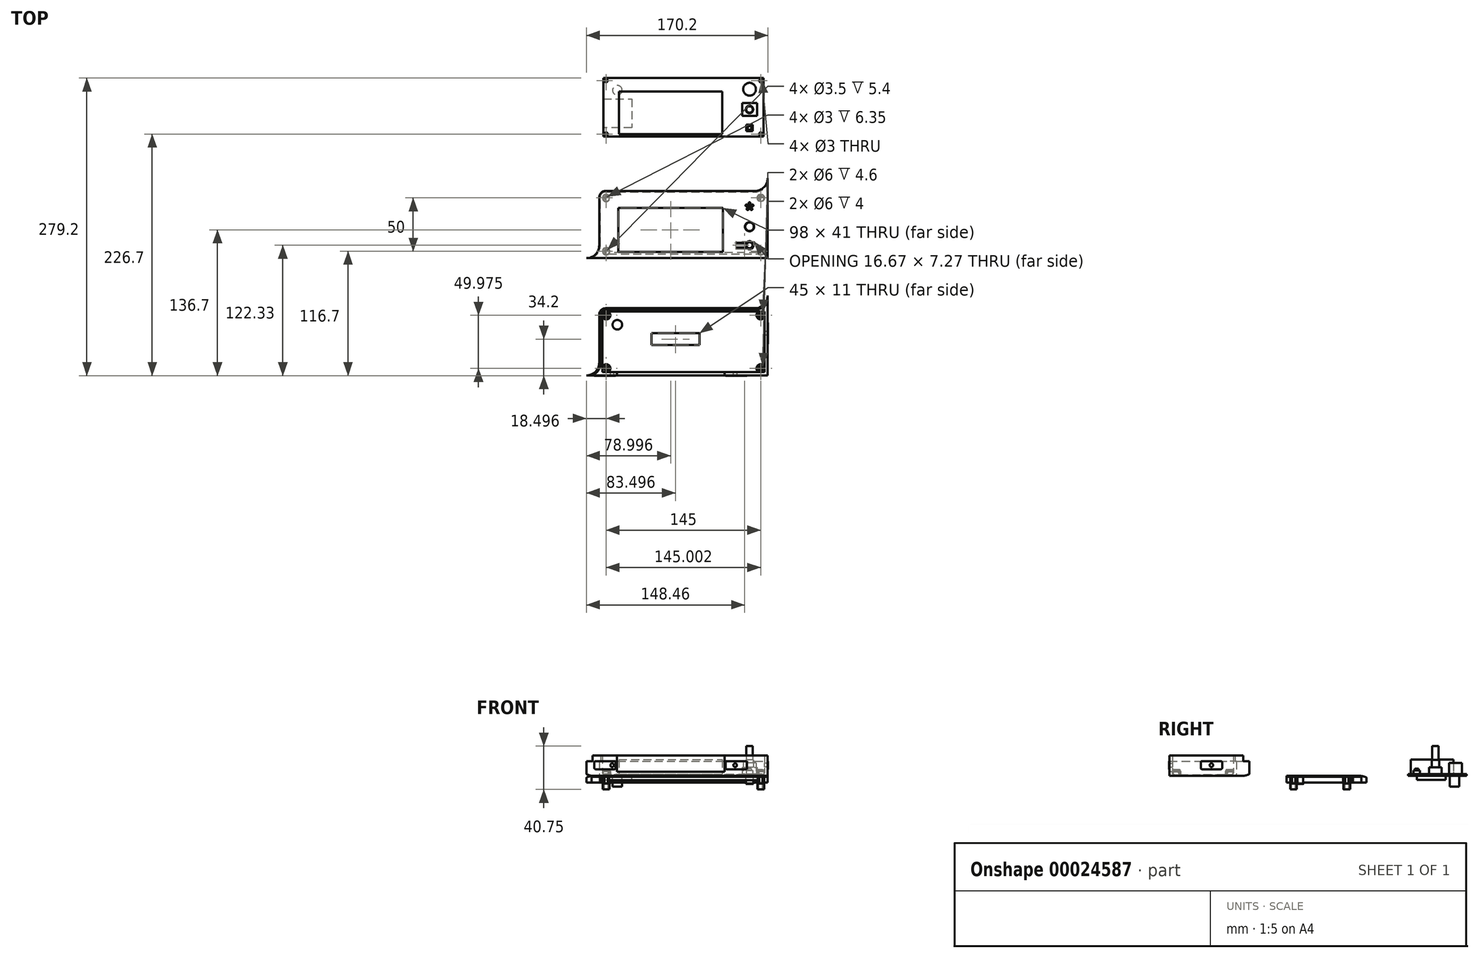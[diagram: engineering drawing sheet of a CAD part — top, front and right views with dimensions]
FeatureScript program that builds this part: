
annotation { "Feature Type Name" : "Feature", "Feature Type Description" : "" }
export const myFeature = defineFeature(function(context is Context, id is Id, definition is map)
    precondition{}
    {
        {
            assignVariable(context, id + "F0", {"name" : "profile_distance_x", "anyValue" : 10 - 7.3 / 2});
        }
        {
            assignVariable(context, id + "F1", {"name" : "plate_thickness", "anyValue" : 1});
        }
        {
            assignVariable(context, id + "F2", {"name" : "lcd_plate_thickness", "anyValue" : 1.5});
        }
        {
            assignVariable(context, id + "F3", {"name" : "lcd_support_dist1", "anyValue" : 10 - 5.5 / 2 - getVariable(context, 'lcd_plate_thickness')});
        }
        {
            assignVariable(context, id + "F4", {"name" : "button_height", "anyValue" : 6.6 - getVariable(context, 'lcd_plate_thickness')});
        }
        {
            var Q0;
            Q0=qCreatedBy(makeId("Top.planeOp"),FACE);
            var sketch = newSketch(context, id + "F5", { "sketchPlane" : qUnion([Q0])});
            skLineSegment(sketch, "E0.bottom", {"start": v(-53.31, -0.5) * mm, "end": v(116.69, -0.5) * mm});
            skLineSegment(sketch, "E0.top", {"start": v(-35.31, 62.5) * mm, "end": v(104.69, 62.5) * mm});
            skLineSegment(sketch, "E0.left", {"start": v(-41.31, 11.5) * mm, "end": v(-41.31, 56.5) * mm});
            skLineSegment(sketch, "E0.right", {"start": v(116.69, -0.5) * mm, "end": v(116.69, 74.5) * mm});
            skArc(sketch, "E1", {"start": v(-53.31, -0.5) * mm, "mid": v(-44.83, 3.01) * mm, "end": v(-41.31, 11.5) * mm});
            skArc(sketch, "E2", {"start": v(-35.31, 62.5) * mm, "mid": v(-39.56, 60.74) * mm, "end": v(-41.31, 56.5) * mm});
            skArc(sketch, "E3", {"start": v(104.69, 62.5) * mm, "mid": v(113.17, 66.01) * mm, "end": v(116.69, 74.5) * mm});
            skLineSegment(sketch, "E4.bottom", {"start": v(-37.31, 58.5) * mm, "end": v(112.69, 58.5) * mm, "construction": true});
            skLineSegment(sketch, "E4.top", {"start": v(-37.31, 3.5) * mm, "end": v(112.69, 3.5) * mm, "construction": true});
            skLineSegment(sketch, "E4.left", {"start": v(-37.31, 58.5) * mm, "end": v(-37.31, 3.5) * mm, "construction": true});
            skLineSegment(sketch, "E4.right", {"start": v(112.69, 58.5) * mm, "end": v(112.69, 3.5) * mm, "construction": true});
            skLineSegment(sketch, "E5", {"start": v(-37.31, 58.5) * mm, "end": v(-37.31, 58.5) * mm});
            skLineSegment(sketch, "E6", {"start": v(37.69, 80.57) * mm, "end": v(37.69, -27.83) * mm, "construction": true});
            skLineSegment(sketch, "E7", {"start": v(-76.03, 31) * mm, "end": v(149.1, 31) * mm, "construction": true});
            skCircle(sketch, "E8", {"center": v(110.19, 56) * mm, "radius": 1.65 * mm});
            skCircle(sketch, "E9.MirrorC", {"center": v(110.19, 6) * mm, "radius": 1.65 * mm});
            skCircle(sketch, "E10.MirrorC", {"center": v(-34.81, 56) * mm, "radius": 1.65 * mm});
            skCircle(sketch, "E11.MirrorC", {"center": v(-34.81, 6) * mm, "radius": 1.65 * mm});
            skLineSegment(sketch, "E12.0", {"start": v(-38.31, 59.5) * mm, "end": v(113.69, 59.5) * mm});
            skLineSegment(sketch, "E12.1", {"start": v(-38.31, 59.5) * mm, "end": v(-38.31, 2.5) * mm});
            skLineSegment(sketch, "E12.2", {"start": v(-38.31, 2.5) * mm, "end": v(113.69, 2.5) * mm});
            skLineSegment(sketch, "E12.3", {"start": v(113.69, 59.5) * mm, "end": v(113.69, 2.5) * mm});
            skCircle(sketch, "E13", {"center": v(-34.81, 56) * mm, "radius": 3.5 * mm});
            skCircle(sketch, "E14", {"center": v(-34.81, 6) * mm, "radius": 3.5 * mm});
            skCircle(sketch, "E15", {"center": v(110.19, 56) * mm, "radius": 3.5 * mm});
            skCircle(sketch, "E16", {"center": v(110.19, 6) * mm, "radius": 3.5 * mm});
            skLineSegment(sketch, "E17", {"start": v(-24.81, 2.5) * mm, "end": v(-24.81, -0.5) * mm});
            skLineSegment(sketch, "E18", {"start": v(76.19, 2.5) * mm, "end": v(76.19, -0.5) * mm});
            skLineSegment(sketch, "E19.bottom", {"start": v(7.69, 39) * mm, "end": v(52.69, 39) * mm});
            skLineSegment(sketch, "E19.top", {"start": v(7.69, 28) * mm, "end": v(52.69, 28) * mm});
            skLineSegment(sketch, "E19.left", {"start": v(7.69, 39) * mm, "end": v(7.69, 28) * mm});
            skLineSegment(sketch, "E19.right", {"start": v(52.69, 39) * mm, "end": v(52.69, 28) * mm});
            skLineSegment(sketch, "E20.0.1.0", {"start": v(-35.31, 172.5) * mm, "end": v(104.69, 172.5) * mm});
            skLineSegment(sketch, "E20.0.1.1", {"start": v(-41.31, 121.5) * mm, "end": v(-41.31, 166.5) * mm});
            skArc(sketch, "E20.0.1.2", {"start": v(-35.31, 172.5) * mm, "mid": v(-39.56, 170.74) * mm, "end": v(-41.31, 166.5) * mm});
            skArc(sketch, "E20.0.1.3", {"start": v(104.69, 172.5) * mm, "mid": v(113.17, 176.01) * mm, "end": v(116.69, 184.5) * mm});
            skLineSegment(sketch, "E20.0.1.4", {"start": v(116.69, 109.5) * mm, "end": v(116.69, 184.5) * mm});
            skLineSegment(sketch, "E20.0.1.5", {"start": v(113.69, 169.5) * mm, "end": v(113.69, 112.5) * mm});
            skLineSegment(sketch, "E20.0.1.6", {"start": v(112.69, 168.5) * mm, "end": v(112.69, 113.5) * mm, "construction": true});
            skLineSegment(sketch, "E20.0.1.7", {"start": v(-37.31, 168.5) * mm, "end": v(112.69, 168.5) * mm, "construction": true});
            skCircle(sketch, "E20.0.1.8", {"center": v(110.19, 166) * mm, "radius": 3.5 * mm});
            skCircle(sketch, "E20.0.1.10", {"center": v(110.19, 116) * mm, "radius": 3.5 * mm});
            skLineSegment(sketch, "E20.0.1.12", {"start": v(-37.31, 113.5) * mm, "end": v(112.69, 113.5) * mm, "construction": true});
            skLineSegment(sketch, "E20.0.1.13", {"start": v(-38.31, 112.5) * mm, "end": v(113.69, 112.5) * mm});
            skLineSegment(sketch, "E20.0.1.14", {"start": v(-53.31, 109.5) * mm, "end": v(116.69, 109.5) * mm});
            skLineSegment(sketch, "E20.0.1.15", {"start": v(-38.31, 169.5) * mm, "end": v(113.69, 169.5) * mm});
            skLineSegment(sketch, "E20.0.1.16", {"start": v(-38.31, 169.5) * mm, "end": v(-38.31, 112.5) * mm});
            skLineSegment(sketch, "E20.0.1.17", {"start": v(-37.31, 168.5) * mm, "end": v(-37.31, 113.5) * mm, "construction": true});
            skCircle(sketch, "E20.0.1.18", {"center": v(-34.81, 166) * mm, "radius": 3.5 * mm});
            skCircle(sketch, "E20.0.1.20", {"center": v(-34.81, 116) * mm, "radius": 3.5 * mm});
            skArc(sketch, "E20.0.1.22", {"start": v(-53.31, 109.5) * mm, "mid": v(-44.83, 113.01) * mm, "end": v(-41.31, 121.5) * mm});
            skLineSegment(sketch, "E20.direction1", {"start": v(-35.31, 62.5) * mm, "end": v(-4, 62.5) * mm, "construction": true});
            skLineSegment(sketch, "E20.direction2", {"start": v(-35.31, 62.5) * mm, "end": v(-35.31, 172.5) * mm, "construction": true});
            skLineSegment(sketch, "E21.bottom", {"start": v(-22.81, 156) * mm, "end": v(74.19, 156) * mm, "construction": true});
            skLineSegment(sketch, "E21.top", {"start": v(-22.81, 116) * mm, "end": v(74.19, 116) * mm, "construction": true});
            skLineSegment(sketch, "E21.left", {"start": v(-22.81, 156) * mm, "end": v(-22.81, 116) * mm, "construction": true});
            skLineSegment(sketch, "E21.right", {"start": v(74.19, 156) * mm, "end": v(74.19, 116) * mm, "construction": true});
            skCircle(sketch, "E22", {"center": v(99.69, 139) * mm, "radius": 4 * mm});
            skLineSegment(sketch, "E23.bottom", {"start": v(96.69, 124.63) * mm, "end": v(102.69, 124.63) * mm, "construction": true});
            skLineSegment(sketch, "E23.top", {"start": v(96.69, 118.63) * mm, "end": v(102.69, 118.63) * mm, "construction": true});
            skLineSegment(sketch, "E23.left", {"start": v(96.69, 124.63) * mm, "end": v(96.69, 118.63) * mm, "construction": true});
            skLineSegment(sketch, "E23.right", {"start": v(102.69, 124.63) * mm, "end": v(102.69, 118.63) * mm, "construction": true});
            skCircle(sketch, "E24", {"center": v(99.69, 121.63) * mm, "radius": 1.75 * mm, "construction": true});
            skLineSegment(sketch, "E25", {"start": v(96.69, 121.63) * mm, "end": v(102.69, 121.63) * mm, "construction": true});
            skLineSegment(sketch, "E26", {"start": v(99.69, 124.63) * mm, "end": v(99.69, 118.63) * mm, "construction": true});
            skCircle(sketch, "E27", {"center": v(99.69, 161) * mm, "radius": 0.6 * mm});
            skCircle(sketch, "E28.1.0", {"center": v(96.83, 158.93) * mm, "radius": 0.6 * mm});
            skCircle(sketch, "E28.2.0", {"center": v(97.92, 155.57) * mm, "radius": 0.6 * mm});
            skCircle(sketch, "E28.3.0", {"center": v(101.45, 155.57) * mm, "radius": 0.6 * mm});
            skCircle(sketch, "E28.4.0", {"center": v(102.54, 158.93) * mm, "radius": 0.6 * mm});
            skPoint(sketch, "E28.center", {"position": v(99.69, 158) * mm});
            skLineSegment(sketch, "E29", {"start": v(99.69, 124.63) * mm, "end": v(99.69, 182.09) * mm, "construction": true});
            skCircle(sketch, "E30", {"center": v(99.69, 158) * mm, "radius": 3 * mm, "construction": true});
            skCircle(sketch, "E31", {"center": v(-34.81, 166) * mm, "radius": 1.5 * mm});
            skCircle(sketch, "E32", {"center": v(-34.81, 116) * mm, "radius": 1.5 * mm});
            skCircle(sketch, "E33", {"center": v(110.19, 166) * mm, "radius": 1.5 * mm});
            skCircle(sketch, "E34", {"center": v(110.19, 116) * mm, "radius": 1.5 * mm});
            skLineSegment(sketch, "E35.bottom", {"start": v(96.81, 123.63) * mm, "end": v(86.81, 123.63) * mm});
            skLineSegment(sketch, "E35.top", {"start": v(96.81, 119.63) * mm, "end": v(86.81, 119.63) * mm});
            skLineSegment(sketch, "E35.left", {"start": v(96.81, 123.63) * mm, "end": v(96.81, 119.63) * mm, "construction": true});
            skPoint(sketch, "E36", {"position": v(96.81, 121.63) * mm});
            skArc(sketch, "E37", {"start": v(96.81, 119.63) * mm, "mid": v(103.19, 121.63) * mm, "end": v(96.81, 123.63) * mm});
            skLineSegment(sketch, "E38.0", {"start": v(96.66, 123.93) * mm, "end": v(86.81, 123.93) * mm});
            skArc(sketch, "E38.1", {"start": v(96.66, 119.33) * mm, "mid": v(103.49, 121.63) * mm, "end": v(96.66, 123.93) * mm});
            skLineSegment(sketch, "E38.2", {"start": v(96.66, 119.33) * mm, "end": v(86.81, 119.33) * mm});
            skLineSegment(sketch, "E39", {"start": v(86.81, 123.63) * mm, "end": v(86.81, 123.93) * mm});
            skLineSegment(sketch, "E40", {"start": v(86.81, 119.33) * mm, "end": v(86.81, 119.63) * mm});
            skArc(sketch, "E41", {"start": v(96.81, 123.63) * mm, "mid": v(96.19, 121.63) * mm, "end": v(96.81, 119.63) * mm});
            skLineSegment(sketch, "E42.0", {"start": v(-23.31, 156.5) * mm, "end": v(74.69, 156.5) * mm});
            skLineSegment(sketch, "E42.1", {"start": v(-23.31, 156.5) * mm, "end": v(-23.31, 115.5) * mm});
            skLineSegment(sketch, "E42.2", {"start": v(-23.31, 115.5) * mm, "end": v(74.69, 115.5) * mm});
            skLineSegment(sketch, "E42.3", {"start": v(74.69, 156.5) * mm, "end": v(74.69, 115.5) * mm});
            skPoint(sketch, "E43.0.1.0", {"position": v(99.69, 268) * mm});
            skCircle(sketch, "E43.0.1.1", {"center": v(110.19, 276) * mm, "radius": 1.5 * mm});
            skCircle(sketch, "E43.0.1.2", {"center": v(110.19, 226) * mm, "radius": 1.5 * mm});
            skCircle(sketch, "E43.0.1.3", {"center": v(-34.81, 276) * mm, "radius": 1.5 * mm});
            skCircle(sketch, "E43.0.1.4", {"center": v(-34.81, 226) * mm, "radius": 1.5 * mm});
            skLineSegment(sketch, "E43.0.1.5", {"start": v(99.69, 234.63) * mm, "end": v(99.69, 228.63) * mm, "construction": true});
            skLineSegment(sketch, "E43.0.1.6", {"start": v(96.69, 231.63) * mm, "end": v(102.69, 231.63) * mm, "construction": true});
            skCircle(sketch, "E43.0.1.7", {"center": v(99.69, 249) * mm, "radius": 4 * mm, "construction": true});
            skLineSegment(sketch, "E43.0.1.8", {"start": v(-37.31, 278.5) * mm, "end": v(112.69, 278.5) * mm, "construction": true});
            skLineSegment(sketch, "E43.0.1.9", {"start": v(-37.31, 223.5) * mm, "end": v(112.69, 223.5) * mm, "construction": true});
            skLineSegment(sketch, "E43.0.1.10", {"start": v(-22.81, 266) * mm, "end": v(74.19, 266) * mm, "construction": true});
            skLineSegment(sketch, "E43.0.1.11", {"start": v(-22.81, 226) * mm, "end": v(74.19, 226) * mm, "construction": true});
            skLineSegment(sketch, "E43.direction1", {"start": v(-34.81, 116) * mm, "end": v(-9.81, 116) * mm, "construction": true});
            skLineSegment(sketch, "E43.direction2", {"start": v(-34.81, 116) * mm, "end": v(-34.81, 226) * mm, "construction": true});
            skLineSegment(sketch, "E44.bottom", {"start": v(-37.31, 278.5) * mm, "end": v(112.69, 278.5) * mm});
            skLineSegment(sketch, "E44.top", {"start": v(-37.31, 223.5) * mm, "end": v(112.69, 223.5) * mm});
            skLineSegment(sketch, "E44.left", {"start": v(-37.31, 278.5) * mm, "end": v(-37.31, 223.5) * mm});
            skLineSegment(sketch, "E44.right", {"start": v(112.69, 278.5) * mm, "end": v(112.69, 223.5) * mm});
            skLineSegment(sketch, "E45.bottom", {"start": v(-22.81, 266) * mm, "end": v(74.19, 266) * mm});
            skLineSegment(sketch, "E45.top", {"start": v(-22.81, 226) * mm, "end": v(74.19, 226) * mm});
            skLineSegment(sketch, "E45.left", {"start": v(-22.81, 266) * mm, "end": v(-22.81, 226) * mm});
            skLineSegment(sketch, "E45.right", {"start": v(74.19, 266) * mm, "end": v(74.19, 226) * mm});
            skLineSegment(sketch, "E46.bottom", {"start": v(96.69, 234.63) * mm, "end": v(102.69, 234.63) * mm});
            skLineSegment(sketch, "E46.top", {"start": v(96.69, 228.63) * mm, "end": v(102.69, 228.63) * mm});
            skLineSegment(sketch, "E46.left", {"start": v(96.69, 234.63) * mm, "end": v(96.69, 228.63) * mm});
            skLineSegment(sketch, "E46.right", {"start": v(102.69, 234.63) * mm, "end": v(102.69, 228.63) * mm});
            skCircle(sketch, "E47", {"center": v(99.69, 231.63) * mm, "radius": 1.75 * mm});
            skCircle(sketch, "E48", {"center": v(99.69, 268) * mm, "radius": 6 * mm});
            skLineSegment(sketch, "E49.bottom", {"start": v(92.69, 255) * mm, "end": v(106.69, 255) * mm});
            skLineSegment(sketch, "E49.top", {"start": v(92.69, 243) * mm, "end": v(106.69, 243) * mm});
            skLineSegment(sketch, "E49.left", {"start": v(92.69, 255) * mm, "end": v(92.69, 243) * mm});
            skLineSegment(sketch, "E49.right", {"start": v(106.69, 255) * mm, "end": v(106.69, 243) * mm});
            skLineSegment(sketch, "E50", {"start": v(99.69, 255) * mm, "end": v(99.69, 243) * mm, "construction": true});
            skLineSegment(sketch, "E51", {"start": v(106.69, 249) * mm, "end": v(92.69, 249) * mm, "construction": true});
            skCircle(sketch, "E52", {"center": v(99.69, 249) * mm, "radius": 3.5 * mm});
            skCircle(sketch, "E53", {"center": v(99.69, 249) * mm, "radius": 3 * mm});
            skLineSegment(sketch, "E54", {"start": v(-37.31, 258.8) * mm, "end": v(-10.81, 258.8) * mm});
            skLineSegment(sketch, "E55", {"start": v(-10.81, 258.8) * mm, "end": v(-10.81, 231.8) * mm});
            skLineSegment(sketch, "E56", {"start": v(-10.81, 231.8) * mm, "end": v(-37.31, 231.8) * mm});
            skCircle(sketch, "E57", {"center": v(-24.31, 267) * mm, "radius": 4.5 * mm});
            skCircle(sketch, "E58", {"center": v(-24.31, 47) * mm, "radius": 4.5 * mm});
            skCircle(sketch, "E59", {"center": v(99.69, 158) * mm, "radius": 0.6 * mm});
            skLineSegment(sketch, "E60.0", {"start": v(-37.91, 169.1) * mm, "end": v(113.29, 169.1) * mm});
            skLineSegment(sketch, "E60.1", {"start": v(-37.91, 169.1) * mm, "end": v(-37.91, 112.9) * mm});
            skLineSegment(sketch, "E60.2", {"start": v(-37.91, 112.9) * mm, "end": v(113.29, 112.9) * mm});
            skLineSegment(sketch, "E60.3", {"start": v(113.29, 169.1) * mm, "end": v(113.29, 112.9) * mm});
            skLineSegment(sketch, "E61", {"start": v(-32.36, 113.5) * mm, "end": v(107.74, 113.5) * mm});
            skLineSegment(sketch, "E62", {"start": v(106.94, 114.7) * mm, "end": v(-31.56, 114.7) * mm});
            skSolve(sketch);
        }
        {
            var Q0;
            Q0=makeQuery(id+"F5.imprint","IMPRINT",FACE,{"disambiguationData":[TD([[makeQuery(id+"F5.imprint","IMPRINT",EDGE,{"derivedFrom":sQuery(id+"F5.wireOp",EDGE,"E0.bottom")}),1.0]])]});
            var Q1;
            Q1=makeQuery(id+"F5.imprint","IMPRINT",FACE,{"disambiguationData":[TD([[makeQuery(id+"F5.imprint","IMPRINT",EDGE,{"derivedFrom":sQuery(id+"F5.wireOp",EDGE,"E8")}),-1.0]])]});
            var Q2;
            {var subQ5=sQuery(id+"F5.wireOp",EDGE,"E12.0");var subQ11=sQuery(id+"F5.wireOp",EDGE,"E13");var subQ15=makeQuery(id+"F5.imprint","INTERSECT",VERTEX,{"derivedFrom":[subQ5,subQ11]});Q2=makeQuery(id+"F5.imprint","IMPRINT",FACE,{"disambiguationData":[TD([[makeQuery(id+"F5.imprint","IMPRINT",EDGE,{"disambiguationData":[TD([[subQ15,-1.0]])],"derivedFrom":subQ5}),-1.0]])]});}
            var Q3;
            Q3=makeQuery(id+"F5.imprint","IMPRINT",FACE,{"disambiguationData":[TD([[makeQuery(id+"F5.imprint","IMPRINT",EDGE,{"derivedFrom":sQuery(id+"F5.wireOp",EDGE,"E10.MirrorC")}),1.0]])]});
            var Q4;
            {var subQ0=sQuery(id+"F5.wireOp",EDGE,"E12.1");var subQ1=sQuery(id+"F5.wireOp",EDGE,"E12.0");var subQ2=makeQuery(id+"F5.imprint","INTERSECT",VERTEX,{"derivedFrom":[subQ1,subQ0]});Q4=makeQuery(id+"F5.imprint","IMPRINT",FACE,{"disambiguationData":[TD([[makeQuery(id+"F5.imprint","IMPRINT",EDGE,{"disambiguationData":[TD([[subQ2,-1.0]])],"derivedFrom":subQ1}),-1.0]])]});}
            var Q5;
            {var subQ0=sQuery(id+"F5.wireOp",EDGE,"E12.2");var subQ1=sQuery(id+"F5.wireOp",EDGE,"E12.1");var subQ2=makeQuery(id+"F5.imprint","INTERSECT",VERTEX,{"derivedFrom":[subQ1,subQ0]});Q5=makeQuery(id+"F5.imprint","IMPRINT",FACE,{"disambiguationData":[TD([[makeQuery(id+"F5.imprint","IMPRINT",EDGE,{"disambiguationData":[TD([[subQ2,1.0]])],"derivedFrom":subQ1}),1.0]])]});}
            var Q6;
            Q6=makeQuery(id+"F5.imprint","IMPRINT",FACE,{"disambiguationData":[TD([[makeQuery(id+"F5.imprint","IMPRINT",EDGE,{"derivedFrom":sQuery(id+"F5.wireOp",EDGE,"E11.MirrorC")}),-1.0]])]});
            var Q7;
            {var subQ0=sQuery(id+"F5.wireOp",EDGE,"E12.3");var subQ1=sQuery(id+"F5.wireOp",EDGE,"E12.0");var subQ2=makeQuery(id+"F5.imprint","INTERSECT",VERTEX,{"derivedFrom":[subQ1,subQ0]});Q7=makeQuery(id+"F5.imprint","IMPRINT",FACE,{"disambiguationData":[TD([[makeQuery(id+"F5.imprint","IMPRINT",EDGE,{"disambiguationData":[TD([[subQ2,1.0]])],"derivedFrom":subQ1}),-1.0]])]});}
            var Q8;
            Q8=makeQuery(id+"F5.imprint","IMPRINT",FACE,{"disambiguationData":[TD([[makeQuery(id+"F5.imprint","IMPRINT",EDGE,{"derivedFrom":sQuery(id+"F5.wireOp",EDGE,"E9.MirrorC")}),1.0]])]});
            var Q9;
            {var subQ0=sQuery(id+"F5.wireOp",EDGE,"E12.3");var subQ1=sQuery(id+"F5.wireOp",EDGE,"E12.2");var subQ2=makeQuery(id+"F5.imprint","INTERSECT",VERTEX,{"derivedFrom":[subQ1,subQ0]});Q9=makeQuery(id+"F5.imprint","IMPRINT",FACE,{"disambiguationData":[TD([[makeQuery(id+"F5.imprint","IMPRINT",EDGE,{"disambiguationData":[TD([[subQ2,1.0]])],"derivedFrom":subQ1}),1.0]])]});}
            var Q10;
            {var subQ0=sQuery(id+"F5.wireOp",EDGE,"E17");Q10=makeQuery(id+"F5.imprint","IMPRINT",FACE,{"disambiguationData":[TD([[makeQuery(id+"F5.imprint","IMPRINT",EDGE,{"derivedFrom":subQ0}),1.0]])]});}
            extrude(context, id + "F6", {"entities" : qUnion([Q0, Q1, Q2, Q3, Q4, Q5, Q6, Q7, Q8, Q9, Q10]), "depth" : (getVariable(context, 'plate_thickness')) * mm});
        }
        {
            var Q0;
            Q0=makeQuery(id+"F5.imprint","IMPRINT",FACE,{"disambiguationData":[TD([[makeQuery(id+"F5.imprint","IMPRINT",EDGE,{"derivedFrom":sQuery(id+"F5.wireOp",EDGE,"E0.bottom")}),1.0]])]});
            extrude(context, id + "F7", {"entities" : qUnion([Q0]), "operationType" : NewBodyOperationType.ADD, "depth" : (20 - getVariable(context, 'profile_distance_x')) * mm});
        }
        {
            var Q0;
            {var subQ0=sQuery(id+"F5.wireOp",EDGE,"E17");Q0=makeQuery(id+"F5.imprint","IMPRINT",FACE,{"disambiguationData":[TD([[makeQuery(id+"F5.imprint","IMPRINT",EDGE,{"derivedFrom":subQ0}),1.0]])]});}
            extrude(context, id + "F8", {"entities" : qUnion([Q0]), "operationType" : NewBodyOperationType.ADD, "depth" : 4 * mm});
        }
        {
            var Q0;
            {var subQ0=sQuery(id+"F5.wireOp",EDGE,"E12.3");var subQ1=sQuery(id+"F5.wireOp",EDGE,"E12.2");var subQ2=makeQuery(id+"F5.imprint","INTERSECT",VERTEX,{"derivedFrom":[subQ1,subQ0]});Q0=makeQuery(id+"F5.imprint","IMPRINT",FACE,{"disambiguationData":[TD([[makeQuery(id+"F5.imprint","IMPRINT",EDGE,{"disambiguationData":[TD([[subQ2,1.0]])],"derivedFrom":subQ1}),1.0]])]});}
            var Q1;
            Q1=makeQuery(id+"F5.imprint","IMPRINT",FACE,{"disambiguationData":[TD([[makeQuery(id+"F5.imprint","IMPRINT",EDGE,{"derivedFrom":sQuery(id+"F5.wireOp",EDGE,"E9.MirrorC")}),1.0]])]});
            var Q2;
            {var subQ0=sQuery(id+"F5.wireOp",EDGE,"E12.3");var subQ1=sQuery(id+"F5.wireOp",EDGE,"E12.0");var subQ2=makeQuery(id+"F5.imprint","INTERSECT",VERTEX,{"derivedFrom":[subQ1,subQ0]});Q2=makeQuery(id+"F5.imprint","IMPRINT",FACE,{"disambiguationData":[TD([[makeQuery(id+"F5.imprint","IMPRINT",EDGE,{"disambiguationData":[TD([[subQ2,1.0]])],"derivedFrom":subQ1}),-1.0]])]});}
            var Q3;
            Q3=makeQuery(id+"F5.imprint","IMPRINT",FACE,{"disambiguationData":[TD([[makeQuery(id+"F5.imprint","IMPRINT",EDGE,{"derivedFrom":sQuery(id+"F5.wireOp",EDGE,"E8")}),-1.0]])]});
            var Q4;
            Q4=makeQuery(id+"F5.imprint","IMPRINT",FACE,{"disambiguationData":[TD([[makeQuery(id+"F5.imprint","IMPRINT",EDGE,{"derivedFrom":sQuery(id+"F5.wireOp",EDGE,"E10.MirrorC")}),1.0]])]});
            var Q5;
            {var subQ0=sQuery(id+"F5.wireOp",EDGE,"E12.1");var subQ1=sQuery(id+"F5.wireOp",EDGE,"E12.0");var subQ2=makeQuery(id+"F5.imprint","INTERSECT",VERTEX,{"derivedFrom":[subQ1,subQ0]});Q5=makeQuery(id+"F5.imprint","IMPRINT",FACE,{"disambiguationData":[TD([[makeQuery(id+"F5.imprint","IMPRINT",EDGE,{"disambiguationData":[TD([[subQ2,-1.0]])],"derivedFrom":subQ1}),-1.0]])]});}
            var Q6;
            {var subQ0=sQuery(id+"F5.wireOp",EDGE,"E12.2");var subQ1=sQuery(id+"F5.wireOp",EDGE,"E12.1");var subQ2=makeQuery(id+"F5.imprint","INTERSECT",VERTEX,{"derivedFrom":[subQ1,subQ0]});Q6=makeQuery(id+"F5.imprint","IMPRINT",FACE,{"disambiguationData":[TD([[makeQuery(id+"F5.imprint","IMPRINT",EDGE,{"disambiguationData":[TD([[subQ2,1.0]])],"derivedFrom":subQ1}),1.0]])]});}
            var Q7;
            Q7=makeQuery(id+"F5.imprint","IMPRINT",FACE,{"disambiguationData":[TD([[makeQuery(id+"F5.imprint","IMPRINT",EDGE,{"derivedFrom":sQuery(id+"F5.wireOp",EDGE,"E11.MirrorC")}),-1.0]])]});
            extrude(context, id + "F9", {"entities" : qUnion([Q0, Q1, Q2, Q3, Q4, Q5, Q6, Q7]), "operationType" : NewBodyOperationType.ADD, "depth" : (getVariable(context, 'lcd_support_dist1')) * mm});
        }
        {
            var Q0;
            Q0=makeQuery(id+"F7.opExtrude","CAP_FACE",FACE,{"disambiguationData":[OSD([sQuery(id+"F5.wireOp",EDGE,"E0.bottom"),sQuery(id+"F5.wireOp",EDGE,"E0.top"),sQuery(id+"F5.wireOp",EDGE,"E0.left"),sQuery(id+"F5.wireOp",EDGE,"E0.right"),sQuery(id+"F5.wireOp",EDGE,"E1"),sQuery(id+"F5.wireOp",EDGE,"E2"),sQuery(id+"F5.wireOp",EDGE,"E3"),sQuery(id+"F5.wireOp",EDGE,"E12.0"),sQuery(id+"F5.wireOp",EDGE,"E12.1"),sQuery(id+"F5.wireOp",EDGE,"E12.2"),sQuery(id+"F5.wireOp",EDGE,"E12.3"),sQuery(id+"F5.wireOp",EDGE,"E17"),sQuery(id+"F5.wireOp",EDGE,"E18")])],"isStart":false});
            var sketch = newSketch(context, id + "F10", { "sketchPlane" : qUnion([Q0])});
            skLineSegment(sketch, "E63.0", {"start": v(-35.31, 62.5) * mm, "end": v(104.69, 62.5) * mm, "construction": true});
            skArc(sketch, "E64.0", {"start": v(-35.31, 62.5) * mm, "mid": v(-39.56, 60.74) * mm, "end": v(-41.31, 56.5) * mm, "construction": true});
            skLineSegment(sketch, "E65.0", {"start": v(-41.31, 11.5) * mm, "end": v(-41.31, 56.5) * mm, "construction": true});
            skArc(sketch, "E66.0", {"start": v(-53.31, -0.5) * mm, "mid": v(-44.83, 3.01) * mm, "end": v(-41.31, 11.5) * mm, "construction": true});
            skArc(sketch, "E67.0", {"start": v(104.69, 62.5) * mm, "mid": v(113.17, 66.01) * mm, "end": v(116.69, 74.5) * mm, "construction": true});
            skArc(sketch, "E68.0", {"start": v(104.69, 61.2) * mm, "mid": v(114.1, 65.1) * mm, "end": v(117.99, 74.5) * mm});
            skArc(sketch, "E68.1", {"start": v(-53.31, -1.8) * mm, "mid": v(-43.9, 2.1) * mm, "end": v(-40.01, 11.5) * mm});
            skLineSegment(sketch, "E68.2", {"start": v(-40.01, 11.5) * mm, "end": v(-40.01, 56.5) * mm});
            skArc(sketch, "E68.3", {"start": v(-35.31, 61.2) * mm, "mid": v(-38.64, 59.82) * mm, "end": v(-40.01, 56.5) * mm});
            skLineSegment(sketch, "E68.4", {"start": v(-35.31, 61.2) * mm, "end": v(104.69, 61.2) * mm});
            skSolve(sketch);
        }
        {
            var Q0;
            {var subQ15=sQuery(id+"F10.wireOp",EDGE,"E68.2");Q0=makeQuery(id+"F10.imprint","IMPRINT",FACE,{"disambiguationData":[TD([[makeQuery(id+"F10.imprint","IMPRINT",EDGE,{"derivedFrom":subQ15}),-1.0]])]});}
            extrude(context, id + "F11", {"entities" : qUnion([Q0]), "operationType" : NewBodyOperationType.ADD, "depth" : (getVariable(context, 'profile_distance_x') - getVariable(context, 'plate_thickness')) * mm});
        }
        {
            var Q0;
            {var subQ0=sQuery(id+"F5.wireOp",EDGE,"E0.bottom");Q0=makeQuery(id+"F7.boolean.opBoolean","MERGE",FACE,{"derivedFrom":[makeQuery(id+"F6.opExtrude","SWEPT_FACE",FACE,{"disambiguationData":[OSD([subQ0])]}),makeQuery(id+"F7.opExtrude","SWEPT_FACE",FACE,{"disambiguationData":[OSD([subQ0])]})]});}
            var sketch = newSketch(context, id + "F12", { "sketchPlane" : qUnion([Q0])});
            skCircle(sketch, "E69", {"center": v(-29.16, 10) * mm, "radius": 1.7 * mm});
            skCircle(sketch, "E70", {"center": v(86.19, 10) * mm, "radius": 1.7 * mm});
            skCircle(sketch, "E71", {"center": v(-29.16, 10) * mm, "radius": 3 * mm, "construction": true});
            skLineSegment(sketch, "E72", {"start": v(-23.5, 10) * mm, "end": v(-50.14, 10) * mm, "construction": true});
            skLineSegment(sketch, "E73.bottom", {"start": v(-45.81, 13.75) * mm, "end": v(-25.81, 13.75) * mm});
            skLineSegment(sketch, "E73.top", {"start": v(-45.81, 6.25) * mm, "end": v(-25.81, 6.25) * mm});
            skLineSegment(sketch, "E73.left", {"start": v(-45.81, 13.75) * mm, "end": v(-45.81, 6.25) * mm});
            skLineSegment(sketch, "E73.right", {"start": v(-25.81, 13.75) * mm, "end": v(-25.81, 6.25) * mm});
            skPoint(sketch, "E74", {"position": v(-45.81, 10) * mm});
            skPoint(sketch, "E74.positionSnap0", {"position": v(-45.81, 10) * mm});
            skPoint(sketch, "E75.visualSharp", {"position": v(-45.81, 13.75) * mm});
            skPoint(sketch, "E76.visualSharp", {"position": v(-25.81, 13.75) * mm});
            skPoint(sketch, "E77.visualSharp", {"position": v(-25.81, 6.25) * mm});
            skPoint(sketch, "E78.visualSharp", {"position": v(-45.81, 6.25) * mm});
            skLineSegment(sketch, "E79.bottom", {"start": v(77.19, 13.75) * mm, "end": v(97.19, 13.75) * mm});
            skLineSegment(sketch, "E79.top", {"start": v(77.19, 6.25) * mm, "end": v(97.19, 6.25) * mm});
            skLineSegment(sketch, "E79.left", {"start": v(77.19, 13.75) * mm, "end": v(77.19, 6.25) * mm});
            skLineSegment(sketch, "E79.right", {"start": v(97.19, 13.75) * mm, "end": v(97.19, 6.25) * mm});
            skLineSegment(sketch, "E80", {"start": v(75.4, 10) * mm, "end": v(102.6, 10) * mm, "construction": true});
            skPoint(sketch, "E81", {"position": v(77.19, 10) * mm});
            skLineSegment(sketch, "E82.0", {"start": v(-36.46, 0) * mm, "end": v(-33.16, 0) * mm, "construction": true});
            skLineSegment(sketch, "E83", {"start": v(-33.16, 0) * mm, "end": v(-33.16, 11.92) * mm, "construction": true});
            skSolve(sketch);
        }
        {
            var Q0;
            Q0=makeQuery(id+"F12.imprint","IMPRINT",FACE,{"disambiguationData":[TD([[makeQuery(id+"F12.imprint","IMPRINT",EDGE,{"derivedFrom":sQuery(id+"F12.wireOp",EDGE,"E69")}),-1.0]])]});
            var Q1;
            Q1=makeQuery(id+"F12.imprint","IMPRINT",FACE,{"disambiguationData":[TD([[makeQuery(id+"F12.imprint","IMPRINT",EDGE,{"derivedFrom":sQuery(id+"F12.wireOp",EDGE,"E70")}),-1.0]])]});
            extrude(context, id + "F13", {"entities" : qUnion([Q0, Q1]), "operationType" : NewBodyOperationType.ADD, "depth" : 0.2 * mm});
        }
        {
            var Q0;
            Q0=makeQuery(id+"F12.imprint","IMPRINT",FACE,{"disambiguationData":[TD([[makeQuery(id+"F12.imprint","IMPRINT",EDGE,{"derivedFrom":sQuery(id+"F12.wireOp",EDGE,"E69")}),1.0]])]});
            var Q1;
            Q1=makeQuery(id+"F12.imprint","IMPRINT",FACE,{"disambiguationData":[TD([[makeQuery(id+"F12.imprint","IMPRINT",EDGE,{"derivedFrom":sQuery(id+"F12.wireOp",EDGE,"E70")}),1.0]])]});
            extrude(context, id + "F14", {"entities" : qUnion([Q0, Q1]), "operationType" : NewBodyOperationType.REMOVE, "endBound" : BoundingType.UP_TO_NEXT, "oppositeDirection" : true, "depth" : 25 * mm});
        }
        {
            var Q0;
            {var subQ0=sQuery(id+"F5.wireOp",EDGE,"E0.right");Q0=makeQuery(id+"F7.boolean.opBoolean","MERGE",FACE,{"derivedFrom":[makeQuery(id+"F6.opExtrude","SWEPT_FACE",FACE,{"disambiguationData":[OSD([subQ0])]}),makeQuery(id+"F7.opExtrude","SWEPT_FACE",FACE,{"disambiguationData":[OSD([subQ0])]})]});}
            var sketch = newSketch(context, id + "F15", { "sketchPlane" : qUnion([Q0])});
            skPoint(sketch, "E84", {"position": v(56, 0) * mm});
            skLineSegment(sketch, "E85", {"start": v(56, -1.1) * mm, "end": v(56, 19.44) * mm, "construction": true});
            skCircle(sketch, "E86", {"center": v(39, 10) * mm, "radius": 1.7 * mm});
            skLineSegment(sketch, "E87", {"start": v(27.9, 10) * mm, "end": v(50.63, 10) * mm, "construction": true});
            skLineSegment(sketch, "E88", {"start": v(39, 14.69) * mm, "end": v(39, 5.42) * mm, "construction": true});
            skLineSegment(sketch, "E89.bottom", {"start": v(29, 13.75) * mm, "end": v(49, 13.75) * mm});
            skLineSegment(sketch, "E89.top", {"start": v(29, 6.25) * mm, "end": v(49, 6.25) * mm});
            skLineSegment(sketch, "E89.left", {"start": v(29, 13.75) * mm, "end": v(29, 6.25) * mm});
            skLineSegment(sketch, "E89.right", {"start": v(49, 13.75) * mm, "end": v(49, 6.25) * mm});
            skPoint(sketch, "E90", {"position": v(29, 10) * mm});
            skPoint(sketch, "E91", {"position": v(39, 13.75) * mm});
            skLineSegment(sketch, "E92.0", {"start": v(54.35, 0) * mm, "end": v(57.65, 0) * mm, "construction": true});
            skSolve(sketch);
        }
        {
            var Q0;
            Q0=makeQuery(id+"F15.imprint","IMPRINT",FACE,{"disambiguationData":[TD([[makeQuery(id+"F15.imprint","IMPRINT",EDGE,{"derivedFrom":sQuery(id+"F15.wireOp",EDGE,"E86")}),-1.0]])]});
            extrude(context, id + "F16", {"entities" : qUnion([Q0]), "operationType" : NewBodyOperationType.ADD, "depth" : 0.2 * mm});
        }
        {
            var Q0;
            Q0=makeQuery(id+"F15.imprint","IMPRINT",FACE,{"disambiguationData":[TD([[makeQuery(id+"F15.imprint","IMPRINT",EDGE,{"derivedFrom":sQuery(id+"F15.wireOp",EDGE,"E86")}),1.0]])]});
            extrude(context, id + "F17", {"entities" : qUnion([Q0]), "operationType" : NewBodyOperationType.REMOVE, "endBound" : BoundingType.UP_TO_NEXT, "oppositeDirection" : true, "depth" : 25 * mm});
        }
        {
            var Q0;
            Q0=makeQuery(id+"F13.opExtrude","SWEPT_EDGE",EDGE,{"disambiguationData":[OSD([sQuery(id+"F12.wireOp",EDGE,"E73.bottom"),sQuery(id+"F12.wireOp",EDGE,"E73.left")])]});
            var Q1;
            Q1=makeQuery(id+"F13.opExtrude","SWEPT_EDGE",EDGE,{"disambiguationData":[OSD([sQuery(id+"F12.wireOp",EDGE,"E73.top"),sQuery(id+"F12.wireOp",EDGE,"E73.left")])]});
            var Q2;
            Q2=makeQuery(id+"F13.opExtrude","SWEPT_EDGE",EDGE,{"disambiguationData":[OSD([sQuery(id+"F12.wireOp",EDGE,"E73.top"),sQuery(id+"F12.wireOp",EDGE,"E73.right")])]});
            var Q3;
            Q3=makeQuery(id+"F13.opExtrude","SWEPT_EDGE",EDGE,{"disambiguationData":[OSD([sQuery(id+"F12.wireOp",EDGE,"E73.bottom"),sQuery(id+"F12.wireOp",EDGE,"E73.right")])]});
            var Q4;
            Q4=makeQuery(id+"F13.opExtrude","SWEPT_EDGE",EDGE,{"disambiguationData":[OSD([sQuery(id+"F12.wireOp",EDGE,"E79.top"),sQuery(id+"F12.wireOp",EDGE,"E79.right")])]});
            var Q5;
            Q5=makeQuery(id+"F13.opExtrude","SWEPT_EDGE",EDGE,{"disambiguationData":[OSD([sQuery(id+"F12.wireOp",EDGE,"E79.bottom"),sQuery(id+"F12.wireOp",EDGE,"E79.right")])]});
            var Q6;
            Q6=makeQuery(id+"F13.opExtrude","SWEPT_EDGE",EDGE,{"disambiguationData":[OSD([sQuery(id+"F12.wireOp",EDGE,"E79.top"),sQuery(id+"F12.wireOp",EDGE,"E79.left")])]});
            var Q7;
            Q7=makeQuery(id+"F13.opExtrude","SWEPT_EDGE",EDGE,{"disambiguationData":[OSD([sQuery(id+"F12.wireOp",EDGE,"E79.bottom"),sQuery(id+"F12.wireOp",EDGE,"E79.left")])]});
            var Q8;
            Q8=makeQuery(id+"F16.opExtrude","SWEPT_EDGE",EDGE,{"disambiguationData":[OSD([sQuery(id+"F15.wireOp",EDGE,"E89.bottom"),sQuery(id+"F15.wireOp",EDGE,"E89.left")])]});
            var Q9;
            Q9=makeQuery(id+"F16.opExtrude","SWEPT_EDGE",EDGE,{"disambiguationData":[OSD([sQuery(id+"F15.wireOp",EDGE,"E89.top"),sQuery(id+"F15.wireOp",EDGE,"E89.left")])]});
            var Q10;
            Q10=makeQuery(id+"F16.opExtrude","SWEPT_EDGE",EDGE,{"disambiguationData":[OSD([sQuery(id+"F15.wireOp",EDGE,"E89.bottom"),sQuery(id+"F15.wireOp",EDGE,"E89.right")])]});
            var Q11;
            Q11=makeQuery(id+"F16.opExtrude","SWEPT_EDGE",EDGE,{"disambiguationData":[OSD([sQuery(id+"F15.wireOp",EDGE,"E89.top"),sQuery(id+"F15.wireOp",EDGE,"E89.right")])]});
            fillet(context, id + "F18", {"entities" : qUnion([Q0, Q1, Q2, Q3, Q4, Q5, Q6, Q7, Q8, Q9, Q10, Q11]), "radius" : 1 * mm, "tangentPropagation" : true, "allowEdgeOverflow" : false});
        }
        {
            var Q0;
            Q0=makeQuery(id+"F5.imprint","IMPRINT",FACE,{"disambiguationData":[TD([[makeQuery(id+"F5.imprint","IMPRINT",EDGE,{"derivedFrom":sQuery(id+"F5.wireOp",EDGE,"E20.0.1.0")}),-1.0]])]});
            var Q1;
            Q1=makeQuery(id+"F5.imprint","IMPRINT",FACE,{"disambiguationData":[TD([[makeQuery(id+"F5.imprint","IMPRINT",EDGE,{"derivedFrom":sQuery(id+"F5.wireOp",EDGE,"E21.bottom")}),1.0]])]});
            var Q2;
            {var subQ0=sQuery(id+"F5.wireOp",EDGE,"E20.0.1.15");var subQ1=sQuery(id+"F5.wireOp",EDGE,"E20.0.1.5");var subQ2=makeQuery(id+"F5.imprint","INTERSECT",VERTEX,{"derivedFrom":[subQ1,subQ0]});Q2=makeQuery(id+"F5.imprint","IMPRINT",FACE,{"disambiguationData":[TD([[makeQuery(id+"F5.imprint","IMPRINT",EDGE,{"disambiguationData":[TD([[subQ2,-1.0]])],"derivedFrom":subQ1}),-1.0]])]});}
            var Q3;
            {var subQ0=sQuery(id+"F5.wireOp",EDGE,"E20.0.1.13");var subQ1=sQuery(id+"F5.wireOp",EDGE,"E20.0.1.5");var subQ2=makeQuery(id+"F5.imprint","INTERSECT",VERTEX,{"derivedFrom":[subQ1,subQ0]});Q3=makeQuery(id+"F5.imprint","IMPRINT",FACE,{"disambiguationData":[TD([[makeQuery(id+"F5.imprint","IMPRINT",EDGE,{"disambiguationData":[TD([[subQ2,1.0]])],"derivedFrom":subQ1}),-1.0]])]});}
            var Q4;
            {var subQ0=sQuery(id+"F5.wireOp",EDGE,"E20.0.1.16");var subQ1=sQuery(id+"F5.wireOp",EDGE,"E20.0.1.13");var subQ2=makeQuery(id+"F5.imprint","INTERSECT",VERTEX,{"derivedFrom":[subQ1,subQ0]});Q4=makeQuery(id+"F5.imprint","IMPRINT",FACE,{"disambiguationData":[TD([[makeQuery(id+"F5.imprint","IMPRINT",EDGE,{"disambiguationData":[TD([[subQ2,-1.0]])],"derivedFrom":subQ1}),1.0]])]});}
            var Q5;
            {var subQ0=sQuery(id+"F5.wireOp",EDGE,"E20.0.1.16");var subQ1=sQuery(id+"F5.wireOp",EDGE,"E20.0.1.15");var subQ2=makeQuery(id+"F5.imprint","INTERSECT",VERTEX,{"derivedFrom":[subQ1,subQ0]});Q5=makeQuery(id+"F5.imprint","IMPRINT",FACE,{"disambiguationData":[TD([[makeQuery(id+"F5.imprint","IMPRINT",EDGE,{"disambiguationData":[TD([[subQ2,-1.0]])],"derivedFrom":subQ1}),-1.0]])]});}
            var Q6;
            Q6=makeQuery(id+"F5.imprint","IMPRINT",FACE,{"disambiguationData":[TD([[makeQuery(id+"F5.imprint","IMPRINT",EDGE,{"derivedFrom":sQuery(id+"F5.wireOp",EDGE,"E31")}),-1.0]])]});
            var Q7;
            Q7=makeQuery(id+"F5.imprint","IMPRINT",FACE,{"disambiguationData":[TD([[makeQuery(id+"F5.imprint","IMPRINT",EDGE,{"derivedFrom":sQuery(id+"F5.wireOp",EDGE,"E31")}),1.0]])]});
            var Q8;
            Q8=makeQuery(id+"F5.imprint","IMPRINT",FACE,{"disambiguationData":[TD([[makeQuery(id+"F5.imprint","IMPRINT",EDGE,{"derivedFrom":sQuery(id+"F5.wireOp",EDGE,"E32")}),-1.0]])]});
            var Q9;
            Q9=makeQuery(id+"F5.imprint","IMPRINT",FACE,{"disambiguationData":[TD([[makeQuery(id+"F5.imprint","IMPRINT",EDGE,{"derivedFrom":sQuery(id+"F5.wireOp",EDGE,"E32")}),1.0]])]});
            var Q10;
            Q10=makeQuery(id+"F5.imprint","IMPRINT",FACE,{"disambiguationData":[TD([[makeQuery(id+"F5.imprint","IMPRINT",EDGE,{"derivedFrom":sQuery(id+"F5.wireOp",EDGE,"E34")}),1.0]])]});
            var Q11;
            Q11=makeQuery(id+"F5.imprint","IMPRINT",FACE,{"disambiguationData":[TD([[makeQuery(id+"F5.imprint","IMPRINT",EDGE,{"derivedFrom":sQuery(id+"F5.wireOp",EDGE,"E34")}),-1.0]])]});
            var Q12;
            Q12=makeQuery(id+"F5.imprint","IMPRINT",FACE,{"disambiguationData":[TD([[makeQuery(id+"F5.imprint","IMPRINT",EDGE,{"derivedFrom":sQuery(id+"F5.wireOp",EDGE,"E33")}),1.0]])]});
            var Q13;
            Q13=makeQuery(id+"F5.imprint","IMPRINT",FACE,{"disambiguationData":[TD([[makeQuery(id+"F5.imprint","IMPRINT",EDGE,{"derivedFrom":sQuery(id+"F5.wireOp",EDGE,"E33")}),-1.0]])]});
            var Q14;
            Q14=makeQuery(id+"F5.imprint","IMPRINT",FACE,{"disambiguationData":[TD([[makeQuery(id+"F5.imprint","IMPRINT",EDGE,{"derivedFrom":sQuery(id+"F5.wireOp",EDGE,"E37")}),1.0]])]});
            var Q15;
            Q15=makeQuery(id+"F5.imprint","IMPRINT",FACE,{"disambiguationData":[TD([[makeQuery(id+"F5.imprint","IMPRINT",EDGE,{"derivedFrom":sQuery(id+"F5.wireOp",EDGE,"E22")}),-1.0]])]});
            var Q16;
            {var subQ0=sQuery(id+"F5.wireOp",EDGE,"E60.0");var subQ1=sQuery(id+"F5.wireOp",EDGE,"E20.0.1.18");var subQ2=makeQuery(id+"F5.imprint","INTERSECT",VERTEX,{"disambiguationData":[OD(1.0)],"derivedFrom":[subQ1,subQ0]});Q16=makeQuery(id+"F5.imprint","IMPRINT",FACE,{"disambiguationData":[TD([[makeQuery(id+"F5.imprint","IMPRINT",EDGE,{"disambiguationData":[TD([[subQ2,-1.0]])],"derivedFrom":subQ1}),-1.0]])]});}
            var Q17;
            {var subQ0=sQuery(id+"F5.wireOp",EDGE,"E20.0.1.18");var subQ1=makeQuery(id+"F5.imprint","INTERSECT",VERTEX,{"derivedFrom":[sQuery(id+"F5.wireOp",EDGE,"E20.0.1.16"),subQ0]});Q17=makeQuery(id+"F5.imprint","IMPRINT",FACE,{"disambiguationData":[TD([[makeQuery(id+"F5.imprint","IMPRINT",EDGE,{"disambiguationData":[TD([[subQ1,1.0]])],"derivedFrom":subQ0}),1.0]])]});}
            var Q18;
            {var subQ0=sQuery(id+"F5.wireOp",EDGE,"E20.0.1.18");var subQ1=sQuery(id+"F5.wireOp",EDGE,"E20.0.1.16");var subQ2=makeQuery(id+"F5.imprint","INTERSECT",VERTEX,{"derivedFrom":[subQ1,subQ0]});Q18=makeQuery(id+"F5.imprint","IMPRINT",FACE,{"disambiguationData":[TD([[makeQuery(id+"F5.imprint","IMPRINT",EDGE,{"disambiguationData":[TD([[subQ2,-1.0]])],"derivedFrom":subQ1}),1.0]])]});}
            var Q19;
            {var subQ0=sQuery(id+"F5.wireOp",EDGE,"E20.0.1.18");var subQ1=makeQuery(id+"F5.imprint","INTERSECT",VERTEX,{"derivedFrom":[sQuery(id+"F5.wireOp",EDGE,"E20.0.1.15"),subQ0]});Q19=makeQuery(id+"F5.imprint","IMPRINT",FACE,{"disambiguationData":[TD([[makeQuery(id+"F5.imprint","IMPRINT",EDGE,{"disambiguationData":[TD([[subQ1,1.0]])],"derivedFrom":subQ0}),1.0]])]});}
            var Q20;
            {var subQ0=sQuery(id+"F5.wireOp",EDGE,"E20.0.1.15");var subQ1=sQuery(id+"F5.wireOp",EDGE,"E20.0.1.8");var subQ2=makeQuery(id+"F5.imprint","INTERSECT",VERTEX,{"derivedFrom":[subQ1,subQ0]});Q20=makeQuery(id+"F5.imprint","IMPRINT",FACE,{"disambiguationData":[TD([[makeQuery(id+"F5.imprint","IMPRINT",EDGE,{"disambiguationData":[TD([[subQ2,-1.0]])],"derivedFrom":subQ1}),-1.0]])]});}
            var Q21;
            {var subQ0=sQuery(id+"F5.wireOp",EDGE,"E60.2");var subQ1=sQuery(id+"F5.wireOp",EDGE,"E20.0.1.10");var subQ2=makeQuery(id+"F5.imprint","INTERSECT",VERTEX,{"disambiguationData":[OD(0.0)],"derivedFrom":[subQ1,subQ0]});Q21=makeQuery(id+"F5.imprint","IMPRINT",FACE,{"disambiguationData":[TD([[makeQuery(id+"F5.imprint","IMPRINT",EDGE,{"disambiguationData":[TD([[subQ2,-1.0]])],"derivedFrom":subQ1}),-1.0]])]});}
            var Q22;
            {var subQ0=sQuery(id+"F5.wireOp",EDGE,"E20.0.1.20");var subQ1=makeQuery(id+"F5.imprint","INTERSECT",VERTEX,{"derivedFrom":[sQuery(id+"F5.wireOp",EDGE,"E20.0.1.13"),subQ0]});Q22=makeQuery(id+"F5.imprint","IMPRINT",FACE,{"disambiguationData":[TD([[makeQuery(id+"F5.imprint","IMPRINT",EDGE,{"disambiguationData":[TD([[subQ1,1.0]])],"derivedFrom":subQ0}),1.0]])]});}
            var Q23;
            {var subQ0=sQuery(id+"F5.wireOp",EDGE,"E60.1");var subQ1=sQuery(id+"F5.wireOp",EDGE,"E20.0.1.20");var subQ2=makeQuery(id+"F5.imprint","INTERSECT",VERTEX,{"disambiguationData":[OD(1.0)],"derivedFrom":[subQ1,subQ0]});Q23=makeQuery(id+"F5.imprint","IMPRINT",FACE,{"disambiguationData":[TD([[makeQuery(id+"F5.imprint","IMPRINT",EDGE,{"disambiguationData":[TD([[subQ2,-1.0]])],"derivedFrom":subQ1}),-1.0]])]});}
            var Q24;
            {var subQ0=sQuery(id+"F5.wireOp",EDGE,"E20.0.1.20");var subQ1=makeQuery(id+"F5.imprint","INTERSECT",VERTEX,{"derivedFrom":[sQuery(id+"F5.wireOp",EDGE,"E20.0.1.16"),subQ0]});Q24=makeQuery(id+"F5.imprint","IMPRINT",FACE,{"disambiguationData":[TD([[makeQuery(id+"F5.imprint","IMPRINT",EDGE,{"disambiguationData":[TD([[subQ1,1.0]])],"derivedFrom":subQ0}),1.0]])]});}
            var Q25;
            {var subQ0=sQuery(id+"F5.wireOp",EDGE,"E60.2");var subQ1=sQuery(id+"F5.wireOp",EDGE,"E20.0.1.10");var subQ2=makeQuery(id+"F5.imprint","INTERSECT",VERTEX,{"disambiguationData":[OD(0.0)],"derivedFrom":[subQ1,subQ0]});Q25=makeQuery(id+"F5.imprint","IMPRINT",FACE,{"disambiguationData":[TD([[makeQuery(id+"F5.imprint","IMPRINT",EDGE,{"disambiguationData":[TD([[subQ2,-1.0]])],"derivedFrom":subQ1}),1.0]])]});}
            var Q26;
            {var subQ0=sQuery(id+"F5.wireOp",EDGE,"E60.2");var subQ1=sQuery(id+"F5.wireOp",EDGE,"E20.0.1.10");var subQ2=makeQuery(id+"F5.imprint","INTERSECT",VERTEX,{"disambiguationData":[OD(1.0)],"derivedFrom":[subQ1,subQ0]});Q26=makeQuery(id+"F5.imprint","IMPRINT",FACE,{"disambiguationData":[TD([[makeQuery(id+"F5.imprint","IMPRINT",EDGE,{"disambiguationData":[TD([[subQ2,-1.0]])],"derivedFrom":subQ1}),-1.0]])]});}
            var Q27;
            {var subQ0=sQuery(id+"F5.wireOp",EDGE,"E20.0.1.10");var subQ1=makeQuery(id+"F5.imprint","INTERSECT",VERTEX,{"derivedFrom":[sQuery(id+"F5.wireOp",EDGE,"E20.0.1.5"),subQ0]});Q27=makeQuery(id+"F5.imprint","IMPRINT",FACE,{"disambiguationData":[TD([[makeQuery(id+"F5.imprint","IMPRINT",EDGE,{"disambiguationData":[TD([[subQ1,-1.0]])],"derivedFrom":subQ0}),1.0]])]});}
            var Q28;
            {var subQ0=sQuery(id+"F5.wireOp",EDGE,"E20.0.1.8");var subQ1=sQuery(id+"F5.wireOp",EDGE,"E20.0.1.5");var subQ2=makeQuery(id+"F5.imprint","INTERSECT",VERTEX,{"derivedFrom":[subQ1,subQ0]});Q28=makeQuery(id+"F5.imprint","IMPRINT",FACE,{"disambiguationData":[TD([[makeQuery(id+"F5.imprint","IMPRINT",EDGE,{"disambiguationData":[TD([[subQ2,-1.0]])],"derivedFrom":subQ1}),-1.0]])]});}
            var Q29;
            {var subQ0=sQuery(id+"F5.wireOp",EDGE,"E20.0.1.8");var subQ1=makeQuery(id+"F5.imprint","INTERSECT",VERTEX,{"derivedFrom":[sQuery(id+"F5.wireOp",EDGE,"E20.0.1.5"),subQ0]});Q29=makeQuery(id+"F5.imprint","IMPRINT",FACE,{"disambiguationData":[TD([[makeQuery(id+"F5.imprint","IMPRINT",EDGE,{"disambiguationData":[TD([[subQ1,-1.0]])],"derivedFrom":subQ0}),1.0]])]});}
            var Q30;
            {var subQ0=sQuery(id+"F5.wireOp",EDGE,"E60.3");var subQ1=sQuery(id+"F5.wireOp",EDGE,"E20.0.1.8");var subQ2=makeQuery(id+"F5.imprint","INTERSECT",VERTEX,{"disambiguationData":[OD(0.0)],"derivedFrom":[subQ1,subQ0]});Q30=makeQuery(id+"F5.imprint","IMPRINT",FACE,{"disambiguationData":[TD([[makeQuery(id+"F5.imprint","IMPRINT",EDGE,{"disambiguationData":[TD([[subQ2,-1.0]])],"derivedFrom":subQ1}),-1.0]])]});}
            var Q31;
            {var subQ0=sQuery(id+"F5.wireOp",EDGE,"E60.0");var subQ1=sQuery(id+"F5.wireOp",EDGE,"E20.0.1.8");var subQ2=makeQuery(id+"F5.imprint","INTERSECT",VERTEX,{"disambiguationData":[OD(0.0)],"derivedFrom":[subQ1,subQ0]});Q31=makeQuery(id+"F5.imprint","IMPRINT",FACE,{"disambiguationData":[TD([[makeQuery(id+"F5.imprint","IMPRINT",EDGE,{"disambiguationData":[TD([[subQ2,-1.0]])],"derivedFrom":subQ1}),1.0]])]});}
            var Q32;
            {var subQ0=sQuery(id+"F5.wireOp",EDGE,"E61");Q32=makeQuery(id+"F5.imprint","IMPRINT",FACE,{"disambiguationData":[TD([[makeQuery(id+"F5.imprint","IMPRINT",EDGE,{"derivedFrom":subQ0}),1.0]])]});}
            var Q33;
            {var subQ0=sQuery(id+"F5.wireOp",EDGE,"E61");Q33=makeQuery(id+"F5.imprint","IMPRINT",FACE,{"disambiguationData":[TD([[makeQuery(id+"F5.imprint","IMPRINT",EDGE,{"derivedFrom":subQ0}),-1.0]])]});}
            extrude(context, id + "F19", {"entities" : qUnion([Q0, Q1, Q2, Q3, Q4, Q5, Q6, Q7, Q8, Q9, Q10, Q11, Q12, Q13, Q14, Q15, Q16, Q17, Q18, Q19, Q20, Q21, Q22, Q23, Q24, Q25, Q26, Q27, Q28, Q29, Q30, Q31, Q32, Q33]), "oppositeDirection" : true, "depth" : (getVariable(context, 'plate_thickness')) * mm});
        }
        {
            var Q0;
            Q0=makeQuery(id+"F19.opExtrude","CAP_FACE",FACE,{"disambiguationData":[OSD([sQuery(id+"F5.wireOp",EDGE,"E20.0.1.0"),sQuery(id+"F5.wireOp",EDGE,"E20.0.1.1"),sQuery(id+"F5.wireOp",EDGE,"E20.0.1.2"),sQuery(id+"F5.wireOp",EDGE,"E20.0.1.3"),sQuery(id+"F5.wireOp",EDGE,"E20.0.1.4"),sQuery(id+"F5.wireOp",EDGE,"E20.0.1.14"),sQuery(id+"F5.wireOp",EDGE,"E20.0.1.22"),sQuery(id+"F5.wireOp",EDGE,"E22"),sQuery(id+"F5.wireOp",EDGE,"E27"),sQuery(id+"F5.wireOp",EDGE,"E28.1.0"),sQuery(id+"F5.wireOp",EDGE,"E28.2.0"),sQuery(id+"F5.wireOp",EDGE,"E28.3.0"),sQuery(id+"F5.wireOp",EDGE,"E28.4.0"),sQuery(id+"F5.wireOp",EDGE,"E35.bottom"),sQuery(id+"F5.wireOp",EDGE,"E35.top"),sQuery(id+"F5.wireOp",EDGE,"E37"),sQuery(id+"F5.wireOp",EDGE,"E38.0"),sQuery(id+"F5.wireOp",EDGE,"E38.1"),sQuery(id+"F5.wireOp",EDGE,"E38.2"),sQuery(id+"F5.wireOp",EDGE,"E39"),sQuery(id+"F5.wireOp",EDGE,"E40"),sQuery(id+"F5.wireOp",EDGE,"E42.0"),sQuery(id+"F5.wireOp",EDGE,"E42.1"),sQuery(id+"F5.wireOp",EDGE,"E42.2"),sQuery(id+"F5.wireOp",EDGE,"E42.3")])],"isStart":false});
            var sketch = newSketch(context, id + "F20", { "sketchPlane" : qUnion([Q0])});
            skArc(sketch, "E93.0", {"start": v(104.69, -171.5) * mm, "mid": v(113.88, -175.3) * mm, "end": v(117.69, -184.5) * mm});
            skArc(sketch, "E93.1", {"start": v(-53.31, -108.5) * mm, "mid": v(-44.12, -112.3) * mm, "end": v(-40.31, -121.5) * mm});
            skLineSegment(sketch, "E93.2", {"start": v(-40.31, -121.5) * mm, "end": v(-40.31, -166.5) * mm});
            skArc(sketch, "E93.3", {"start": v(-35.31, -171.5) * mm, "mid": v(-38.85, -170.04) * mm, "end": v(-40.31, -166.5) * mm});
            skLineSegment(sketch, "E93.4", {"start": v(-35.31, -171.5) * mm, "end": v(104.69, -171.5) * mm});
            skSolve(sketch);
        }
        {
            var Q0;
            {var subQ6=sQuery(id+"F20.wireOp",EDGE,"E93.2");Q0=makeQuery(id+"F20.imprint","IMPRINT",FACE,{"disambiguationData":[TD([[makeQuery(id+"F20.imprint","IMPRINT",EDGE,{"derivedFrom":subQ6}),-1.0]])]});}
            extrude(context, id + "F21", {"entities" : qUnion([Q0]), "operationType" : NewBodyOperationType.ADD, "depth" : (getVariable(context, 'profile_distance_x') - getVariable(context, 'plate_thickness')) * mm});
        }
        {
            var Q0;
            {var subQ0=sQuery(id+"F5.wireOp",EDGE,"E61");Q0=makeQuery(id+"F5.imprint","IMPRINT",FACE,{"disambiguationData":[TD([[makeQuery(id+"F5.imprint","IMPRINT",EDGE,{"derivedFrom":subQ0}),1.0]])]});}
            extrude(context, id + "F22", {"entities" : qUnion([Q0]), "operationType" : NewBodyOperationType.ADD, "oppositeDirection" : true, "depth" : 4 * mm});
        }
        {
            var Q0;
            Q0=makeQuery(id+"F5.imprint","IMPRINT",FACE,{"disambiguationData":[TD([[makeQuery(id+"F5.imprint","IMPRINT",EDGE,{"derivedFrom":sQuery(id+"F5.wireOp",EDGE,"E34")}),-1.0]])]});
            var Q1;
            Q1=makeQuery(id+"F5.imprint","IMPRINT",FACE,{"disambiguationData":[TD([[makeQuery(id+"F5.imprint","IMPRINT",EDGE,{"derivedFrom":sQuery(id+"F5.wireOp",EDGE,"E33")}),-1.0]])]});
            var Q2;
            Q2=makeQuery(id+"F5.imprint","IMPRINT",FACE,{"disambiguationData":[TD([[makeQuery(id+"F5.imprint","IMPRINT",EDGE,{"derivedFrom":sQuery(id+"F5.wireOp",EDGE,"E31")}),-1.0]])]});
            var Q3;
            Q3=makeQuery(id+"F5.imprint","IMPRINT",FACE,{"disambiguationData":[TD([[makeQuery(id+"F5.imprint","IMPRINT",EDGE,{"derivedFrom":sQuery(id+"F5.wireOp",EDGE,"E32")}),-1.0]])]});
            extrude(context, id + "F23", {"entities" : qUnion([Q0, Q1, Q2, Q3]), "operationType" : NewBodyOperationType.ADD, "oppositeDirection" : true, "depth" : (getVariable(context, 'profile_distance_x') + 1) * mm});
        }
        {
            var Q0;
            Q0=makeQuery(id+"F23.opExtrude","CAP_FACE",FACE,{"disambiguationData":[OSD([sQuery(id+"F5.wireOp",EDGE,"E20.0.1.8"),sQuery(id+"F5.wireOp",EDGE,"E33")])],"isStart":false});
            var sketch = newSketch(context, id + "F24", { "sketchPlane" : qUnion([Q0])});
            skCircle(sketch, "E94", {"center": v(110.19, -166) * mm, "radius": 1.75 * mm});
            skPoint(sketch, "E95.0", {"position": v(110.19, -116) * mm});
            skPoint(sketch, "E96.0", {"position": v(-34.81, -116) * mm});
            skPoint(sketch, "E97.0", {"position": v(-34.81, -166) * mm});
            skCircle(sketch, "E98", {"center": v(-34.81, -166) * mm, "radius": 1.75 * mm});
            skCircle(sketch, "E99", {"center": v(-34.81, -116) * mm, "radius": 1.75 * mm});
            skCircle(sketch, "E100", {"center": v(110.19, -116) * mm, "radius": 1.75 * mm});
            skCircle(sketch, "E101", {"center": v(110.19, -166) * mm, "radius": 3.1 * mm});
            skCircle(sketch, "E102", {"center": v(110.19, -116) * mm, "radius": 3.1 * mm});
            skCircle(sketch, "E103", {"center": v(-34.81, -166) * mm, "radius": 3.1 * mm});
            skCircle(sketch, "E104", {"center": v(-34.81, -116) * mm, "radius": 3.1 * mm});
            skSolve(sketch);
        }
        {
            var Q0;
            Q0=makeQuery(id+"F24.imprint","IMPRINT",FACE,{"disambiguationData":[TD([[makeQuery(id+"F24.imprint","IMPRINT",EDGE,{"derivedFrom":sQuery(id+"F24.wireOp",EDGE,"E94")}),-1.0]])]});
            var Q1;
            Q1=makeQuery(id+"F24.imprint","IMPRINT",FACE,{"disambiguationData":[TD([[makeQuery(id+"F24.imprint","IMPRINT",EDGE,{"derivedFrom":sQuery(id+"F24.wireOp",EDGE,"E100")}),-1.0]])]});
            var Q2;
            Q2=makeQuery(id+"F24.imprint","IMPRINT",FACE,{"disambiguationData":[TD([[makeQuery(id+"F24.imprint","IMPRINT",EDGE,{"derivedFrom":sQuery(id+"F24.wireOp",EDGE,"E98")}),-1.0]])]});
            var Q3;
            Q3=makeQuery(id+"F24.imprint","IMPRINT",FACE,{"disambiguationData":[TD([[makeQuery(id+"F24.imprint","IMPRINT",EDGE,{"derivedFrom":sQuery(id+"F24.wireOp",EDGE,"E99")}),-1.0]])]});
            extrude(context, id + "F25", {"entities" : qUnion([Q0, Q1, Q2, Q3]), "operationType" : NewBodyOperationType.ADD, "depth" : (20 - getVariable(context, 'lcd_support_dist1') - getVariable(context, 'lcd_plate_thickness') - getVariable(context, 'profile_distance_x') - 1) * mm});
        }
        {
            var Q0;
            Q0=makeQuery(id+"F5.imprint","IMPRINT",FACE,{"disambiguationData":[TD([[makeQuery(id+"F5.imprint","IMPRINT",EDGE,{"derivedFrom":sQuery(id+"F5.wireOp",EDGE,"E37")}),1.0]])]});
            extrude(context, id + "F26", {"entities" : qUnion([Q0]), "operationType" : NewBodyOperationType.ADD, "oppositeDirection" : true, "depth" : (20 - getVariable(context, 'lcd_support_dist1') - 6.6) * mm});
        }
        {
            var Q0;
            Q0=sQuery(id+"F5.wireOp",EDGE,"E29");
            cPlane(context, id + "F27", {"entities" : qUnion([Q0]), "cplaneType" : CPlaneType.LINE_ANGLE, "offset" : 25 * mm, "angle" : 90 * degree, "width" : 150 * mm, "height" : 150 * mm});
        }
        {
            var Q0;
            Q0=qCreatedBy(id+"F27.planeOp",FACE);
            var sketch = newSketch(context, id + "F28", { "sketchPlane" : qUnion([Q0])});
            skLineSegment(sketch, "E105.0", {"start": v(118.13, 0) * mm, "end": v(118.83, 0) * mm, "construction": true});
            skLineSegment(sketch, "E106", {"start": v(121.63, 0) * mm, "end": v(121.63, -1.14) * mm, "construction": true});
            skArc(sketch, "E107", {"start": v(118.83, 0) * mm, "mid": v(120.17, -0.66) * mm, "end": v(121.63, -1) * mm});
            skPoint(sketch, "E108", {"position": v(121.63, -1) * mm});
            skLineSegment(sketch, "E109", {"start": v(118.83, 0) * mm, "end": v(125.83, 0) * mm});
            skLineSegment(sketch, "E110", {"start": v(121.63, 0) * mm, "end": v(121.63, -1) * mm});
            skArc(sketch, "E111", {"start": v(121.63, -1) * mm, "mid": v(123.82, -0.86) * mm, "end": v(125.83, 0) * mm, "construction": true});
            skLineSegment(sketch, "E112", {"start": v(125.13, 0) * mm, "end": v(125.83, 0) * mm, "construction": true});
            skLineSegment(sketch, "E113", {"start": v(118.83, 0) * mm, "end": v(125.83, 0) * mm, "construction": true});
            skSolve(sketch);
        }
        {
            var Q0;
            Q0=makeQuery(id+"F28.imprint","IMPRINT",FACE,{"disambiguationData":[TD([[makeQuery(id+"F28.imprint","IMPRINT",EDGE,{"derivedFrom":sQuery(id+"F28.wireOp",EDGE,"E107")}),1.0]])]});
            var Q1;
            Q1=sQuery(id+"F28.wireOp",EDGE,"E106");
            revolve(context, id + "F29", {"operationType" : NewBodyOperationType.REMOVE, "entities" : qUnion([Q0]), "axis" : qUnion([Q1]), "revolveType" : RevolveType.FULL, "oppositeDirection" : true});
        }
        {
            var Q0;
            Q0=makeQuery(id+"F5.imprint","IMPRINT",FACE,{"disambiguationData":[TD([[makeQuery(id+"F5.imprint","IMPRINT",EDGE,{"derivedFrom":sQuery(id+"F5.wireOp",EDGE,"E43.0.1.1")}),-1.0]])]});
            var Q1;
            Q1=makeQuery(id+"F5.imprint","IMPRINT",FACE,{"disambiguationData":[TD([[makeQuery(id+"F5.imprint","IMPRINT",EDGE,{"derivedFrom":sQuery(id+"F5.wireOp",EDGE,"E46.bottom")}),-1.0]])]});
            var Q2;
            Q2=makeQuery(id+"F5.imprint","IMPRINT",FACE,{"disambiguationData":[TD([[makeQuery(id+"F5.imprint","IMPRINT",EDGE,{"derivedFrom":sQuery(id+"F5.wireOp",EDGE,"E49.bottom")}),-1.0]])]});
            var Q3;
            Q3=makeQuery(id+"F5.imprint","IMPRINT",FACE,{"disambiguationData":[TD([[makeQuery(id+"F5.imprint","IMPRINT",EDGE,{"derivedFrom":sQuery(id+"F5.wireOp",EDGE,"E52")}),1.0]])]});
            var Q4;
            Q4=makeQuery(id+"F5.imprint","IMPRINT",FACE,{"disambiguationData":[TD([[makeQuery(id+"F5.imprint","IMPRINT",EDGE,{"derivedFrom":sQuery(id+"F5.wireOp",EDGE,"E48")}),1.0]])]});
            var Q5;
            Q5=makeQuery(id+"F5.imprint","IMPRINT",FACE,{"disambiguationData":[TD([[makeQuery(id+"F5.imprint","IMPRINT",EDGE,{"derivedFrom":sQuery(id+"F5.wireOp",EDGE,"E47")}),1.0]])]});
            var Q6;
            {var subQ0=sQuery(id+"F5.wireOp",EDGE,"E54");Q6=makeQuery(id+"F5.imprint","IMPRINT",FACE,{"disambiguationData":[TD([[makeQuery(id+"F5.imprint","IMPRINT",EDGE,{"derivedFrom":subQ0}),-1.0]])]});}
            var Q7;
            Q7=makeQuery(id+"F5.imprint","IMPRINT",FACE,{"disambiguationData":[TD([[makeQuery(id+"F5.imprint","IMPRINT",EDGE,{"derivedFrom":sQuery(id+"F5.wireOp",EDGE,"E57")}),1.0]])]});
            extrude(context, id + "F30", {"entities" : qUnion([Q0, Q1, Q2, Q3, Q4, Q5, Q6, Q7]), "depth" : (getVariable(context, 'lcd_plate_thickness')) * mm});
        }
        {
            var Q0;
            {var subQ5=sQuery(id+"F5.wireOp",EDGE,"E55");Q0=makeQuery(id+"F5.imprint","IMPRINT",FACE,{"disambiguationData":[TD([[makeQuery(id+"F5.imprint","IMPRINT",EDGE,{"derivedFrom":subQ5}),-1.0]])]});}
            var Q1;
            {var subQ1=sQuery(id+"F5.wireOp",EDGE,"E45.top");Q1=makeQuery(id+"F5.imprint","IMPRINT",FACE,{"disambiguationData":[TD([[makeQuery(id+"F5.imprint","IMPRINT",EDGE,{"derivedFrom":subQ1}),1.0]])]});}
            var Q2;
            {var subQ0=sQuery(id+"F5.wireOp",EDGE,"E45.left");var subQ1=sQuery(id+"F5.wireOp",EDGE,"E45.bottom");var subQ2=makeQuery(id+"F5.imprint","INTERSECT",VERTEX,{"derivedFrom":[subQ1,subQ0]});Q2=makeQuery(id+"F5.imprint","IMPRINT",FACE,{"disambiguationData":[TD([[makeQuery(id+"F5.imprint","IMPRINT",EDGE,{"disambiguationData":[TD([[subQ2,-1.0]])],"derivedFrom":subQ1}),-1.0]])]});}
            extrude(context, id + "F31", {"entities" : qUnion([Q0, Q1, Q2]), "operationType" : NewBodyOperationType.ADD, "depth" : 15.3 * mm});
        }
        {
            var Q0;
            Q0=makeQuery(id+"F5.imprint","IMPRINT",FACE,{"disambiguationData":[TD([[makeQuery(id+"F5.imprint","IMPRINT",EDGE,{"derivedFrom":sQuery(id+"F5.wireOp",EDGE,"E46.bottom")}),-1.0]])]});
            extrude(context, id + "F32", {"entities" : qUnion([Q0]), "operationType" : NewBodyOperationType.ADD, "depth" : 5.1 * mm});
        }
        {
            var Q0;
            Q0=makeQuery(id+"F5.imprint","IMPRINT",FACE,{"disambiguationData":[TD([[makeQuery(id+"F5.imprint","IMPRINT",EDGE,{"derivedFrom":sQuery(id+"F5.wireOp",EDGE,"E47")}),1.0]])]});
            extrude(context, id + "F33", {"entities" : qUnion([Q0]), "operationType" : NewBodyOperationType.ADD, "depth" : (getVariable(context, 'button_height') + getVariable(context, 'lcd_plate_thickness')) * mm});
        }
        {
            var Q0;
            Q0=makeQuery(id+"F5.imprint","IMPRINT",FACE,{"disambiguationData":[TD([[makeQuery(id+"F5.imprint","IMPRINT",EDGE,{"derivedFrom":sQuery(id+"F5.wireOp",EDGE,"E49.bottom")}),-1.0]])]});
            extrude(context, id + "F34", {"entities" : qUnion([Q0]), "operationType" : NewBodyOperationType.ADD, "depth" : 8 * mm});
        }
        {
            var Q0;
            Q0=makeQuery(id+"F5.imprint","IMPRINT",FACE,{"disambiguationData":[TD([[makeQuery(id+"F5.imprint","IMPRINT",EDGE,{"derivedFrom":sQuery(id+"F5.wireOp",EDGE,"E52")}),1.0]])]});
            extrude(context, id + "F35", {"entities" : qUnion([Q0]), "operationType" : NewBodyOperationType.ADD, "depth" : 15 * mm});
        }
        {
            var Q0;
            Q0=makeQuery(id+"F5.imprint","IMPRINT",FACE,{"disambiguationData":[TD([[makeQuery(id+"F5.imprint","IMPRINT",EDGE,{"derivedFrom":sQuery(id+"F5.wireOp",EDGE,"E53")}),1.0]])]});
            extrude(context, id + "F36", {"entities" : qUnion([Q0]), "operationType" : NewBodyOperationType.ADD, "depth" : 28 * mm});
        }
        {
            var Q0;
            Q0=makeQuery(id+"F5.imprint","IMPRINT",FACE,{"disambiguationData":[TD([[makeQuery(id+"F5.imprint","IMPRINT",EDGE,{"derivedFrom":sQuery(id+"F5.wireOp",EDGE,"E48")}),1.0]])]});
            extrude(context, id + "F37", {"entities" : qUnion([Q0]), "operationType" : NewBodyOperationType.ADD, "depth" : 12 * mm});
        }
        {
            var Q0;
            {var subQ0=sQuery(id+"F5.wireOp",EDGE,"E54");Q0=makeQuery(id+"F5.imprint","IMPRINT",FACE,{"disambiguationData":[TD([[makeQuery(id+"F5.imprint","IMPRINT",EDGE,{"derivedFrom":subQ0}),-1.0]])]});}
            extrude(context, id + "F38", {"entities" : qUnion([Q0]), "operationType" : NewBodyOperationType.ADD, "oppositeDirection" : true, "depth" : (5.2 - getVariable(context, 'lcd_plate_thickness')) * mm});
        }
        {
            var Q0;
            Q0=makeQuery(id+"F5.imprint","IMPRINT",FACE,{"disambiguationData":[TD([[makeQuery(id+"F5.imprint","IMPRINT",EDGE,{"derivedFrom":sQuery(id+"F5.wireOp",EDGE,"E57")}),1.0]])]});
            extrude(context, id + "F39", {"entities" : qUnion([Q0]), "operationType" : NewBodyOperationType.ADD, "oppositeDirection" : true, "depth" : 10 * mm});
        }
        {
            var Q0;
            Q0=qCreatedBy(makeId("Top.planeOp"),FACE);
            var sketch = newSketch(context, id + "F40", { "sketchPlane" : qUnion([Q0])});
            skCircle(sketch, "E114", {"center": v(110.19, 55.97) * mm, "radius": 3 * mm});
            skPoint(sketch, "E115.0", {"position": v(-34.81, 6) * mm});
            skPoint(sketch, "E116.0", {"position": v(-34.81, 56) * mm});
            skPoint(sketch, "E117.0", {"position": v(110.19, 6) * mm});
            skCircle(sketch, "E118", {"center": v(110.19, 6) * mm, "radius": 3 * mm});
            skCircle(sketch, "E119", {"center": v(-34.81, 56) * mm, "radius": 3 * mm});
            skCircle(sketch, "E120", {"center": v(-34.81, 6) * mm, "radius": 3 * mm});
            skCircle(sketch, "E121", {"center": v(110.19, 6) * mm, "radius": 4 * mm});
            skCircle(sketch, "E122", {"center": v(110.19, 55.97) * mm, "radius": 4 * mm});
            skCircle(sketch, "E123", {"center": v(-34.81, 56) * mm, "radius": 4 * mm});
            skCircle(sketch, "E124", {"center": v(-34.81, 6) * mm, "radius": 4 * mm});
            skSolve(sketch);
        }
        {
            var Q0;
            Q0=makeQuery(id+"F40.imprint","IMPRINT",FACE,{"disambiguationData":[TD([[makeQuery(id+"F40.imprint","IMPRINT",EDGE,{"derivedFrom":sQuery(id+"F40.wireOp",EDGE,"E119")}),-1.0]])]});
            var Q1;
            Q1=makeQuery(id+"F40.imprint","IMPRINT",FACE,{"disambiguationData":[TD([[makeQuery(id+"F40.imprint","IMPRINT",EDGE,{"derivedFrom":sQuery(id+"F40.wireOp",EDGE,"E120")}),-1.0]])]});
            var Q2;
            Q2=makeQuery(id+"F40.imprint","IMPRINT",FACE,{"disambiguationData":[TD([[makeQuery(id+"F40.imprint","IMPRINT",EDGE,{"derivedFrom":sQuery(id+"F40.wireOp",EDGE,"E118")}),-1.0]])]});
            var Q3;
            Q3=makeQuery(id+"F40.imprint","IMPRINT",FACE,{"disambiguationData":[TD([[makeQuery(id+"F40.imprint","IMPRINT",EDGE,{"derivedFrom":sQuery(id+"F40.wireOp",EDGE,"E114")}),-1.0]])]});
            extrude(context, id + "F41", {"entities" : qUnion([Q0, Q1, Q2, Q3]), "operationType" : NewBodyOperationType.ADD, "depth" : 4.6 * mm});
        }
        {
            var Q0;
            Q0=makeQuery(id+"F40.imprint","IMPRINT",FACE,{"disambiguationData":[TD([[makeQuery(id+"F40.imprint","IMPRINT",EDGE,{"derivedFrom":sQuery(id+"F40.wireOp",EDGE,"E114")}),1.0]])]});
            var Q1;
            Q1=makeQuery(id+"F40.imprint","IMPRINT",FACE,{"disambiguationData":[TD([[makeQuery(id+"F40.imprint","IMPRINT",EDGE,{"derivedFrom":sQuery(id+"F40.wireOp",EDGE,"E118")}),1.0]])]});
            var Q2;
            Q2=makeQuery(id+"F40.imprint","IMPRINT",FACE,{"disambiguationData":[TD([[makeQuery(id+"F40.imprint","IMPRINT",EDGE,{"derivedFrom":sQuery(id+"F40.wireOp",EDGE,"E120")}),1.0]])]});
            var Q3;
            Q3=makeQuery(id+"F40.imprint","IMPRINT",FACE,{"disambiguationData":[TD([[makeQuery(id+"F40.imprint","IMPRINT",EDGE,{"derivedFrom":sQuery(id+"F40.wireOp",EDGE,"E119")}),1.0]])]});
            extrude(context, id + "F42", {"entities" : qUnion([Q0, Q1, Q2, Q3]), "operationType" : NewBodyOperationType.REMOVE, "depth" : 4 * mm});
        }
        {
            var Q0;
            Q0=makeQuery(id+"F19.opExtrude","CAP_EDGE",EDGE,{"disambiguationData":[OSD([sQuery(id+"F5.wireOp",EDGE,"E20.0.1.3")])],"isStart":true});
            var Q1;
            Q1=makeQuery(id+"F19.opExtrude","CAP_EDGE",EDGE,{"disambiguationData":[OSD([sQuery(id+"F5.wireOp",EDGE,"E20.0.1.0")])],"isStart":true});
            var Q2;
            Q2=makeQuery(id+"F19.opExtrude","CAP_EDGE",EDGE,{"disambiguationData":[OSD([sQuery(id+"F5.wireOp",EDGE,"E20.0.1.2")])],"isStart":true});
            var Q3;
            Q3=makeQuery(id+"F19.opExtrude","CAP_EDGE",EDGE,{"disambiguationData":[OSD([sQuery(id+"F5.wireOp",EDGE,"E20.0.1.1")])],"isStart":true});
            var Q4;
            Q4=makeQuery(id+"F19.opExtrude","CAP_EDGE",EDGE,{"disambiguationData":[OSD([sQuery(id+"F5.wireOp",EDGE,"E20.0.1.22")])],"isStart":true});
            var Q5;
            Q5=makeQuery(id+"F6.opExtrude","CAP_EDGE",EDGE,{"disambiguationData":[OSD([sQuery(id+"F5.wireOp",EDGE,"E0.top")])],"isStart":true});
            var Q6;
            Q6=makeQuery(id+"F6.opExtrude","CAP_EDGE",EDGE,{"disambiguationData":[OSD([sQuery(id+"F5.wireOp",EDGE,"E3")])],"isStart":true});
            var Q7;
            Q7=makeQuery(id+"F6.opExtrude","CAP_EDGE",EDGE,{"disambiguationData":[OSD([sQuery(id+"F5.wireOp",EDGE,"E2")])],"isStart":true});
            var Q8;
            Q8=makeQuery(id+"F6.opExtrude","CAP_EDGE",EDGE,{"disambiguationData":[OSD([sQuery(id+"F5.wireOp",EDGE,"E0.left")])],"isStart":true});
            var Q9;
            Q9=makeQuery(id+"F6.opExtrude","CAP_EDGE",EDGE,{"disambiguationData":[OSD([sQuery(id+"F5.wireOp",EDGE,"E1")])],"isStart":true});
            fillet(context, id + "F43", {"entities" : qUnion([Q0, Q1, Q2, Q3, Q4, Q5, Q6, Q7, Q8, Q9]), "radius" : 1.5 * mm, "allowEdgeOverflow" : false});
        }
        {
            var Q0;
            Q0=makeQuery(id+"F7.boolean.opBoolean","INTERSECT",EDGE,{"derivedFrom":[makeQuery(id+"F6.opExtrude","CAP_FACE",FACE,{"disambiguationData":[OSD([sQuery(id+"F5.wireOp",EDGE,"E0.bottom"),sQuery(id+"F5.wireOp",EDGE,"E0.top"),sQuery(id+"F5.wireOp",EDGE,"E0.left"),sQuery(id+"F5.wireOp",EDGE,"E0.right"),sQuery(id+"F5.wireOp",EDGE,"E1"),sQuery(id+"F5.wireOp",EDGE,"E2"),sQuery(id+"F5.wireOp",EDGE,"E3"),sQuery(id+"F5.wireOp",EDGE,"E8"),sQuery(id+"F5.wireOp",EDGE,"E9.MirrorC"),sQuery(id+"F5.wireOp",EDGE,"E10.MirrorC"),sQuery(id+"F5.wireOp",EDGE,"E11.MirrorC"),sQuery(id+"F5.wireOp",EDGE,"E19.bottom"),sQuery(id+"F5.wireOp",EDGE,"E19.top"),sQuery(id+"F5.wireOp",EDGE,"E19.left"),sQuery(id+"F5.wireOp",EDGE,"E19.right"),sQuery(id+"F5.wireOp",EDGE,"E58")])],"isStart":false}),makeQuery(id+"F7.opExtrude","SWEPT_FACE",FACE,{"disambiguationData":[OSD([sQuery(id+"F5.wireOp",EDGE,"E12.0")])]})]});
            var Q1;
            Q1=makeQuery(id+"F9.boolean.opBoolean","INTERSECT",EDGE,{"derivedFrom":[makeQuery(id+"F6.opExtrude","CAP_FACE",FACE,{"disambiguationData":[OSD([sQuery(id+"F5.wireOp",EDGE,"E0.bottom"),sQuery(id+"F5.wireOp",EDGE,"E0.top"),sQuery(id+"F5.wireOp",EDGE,"E0.left"),sQuery(id+"F5.wireOp",EDGE,"E0.right"),sQuery(id+"F5.wireOp",EDGE,"E1"),sQuery(id+"F5.wireOp",EDGE,"E2"),sQuery(id+"F5.wireOp",EDGE,"E3"),sQuery(id+"F5.wireOp",EDGE,"E8"),sQuery(id+"F5.wireOp",EDGE,"E9.MirrorC"),sQuery(id+"F5.wireOp",EDGE,"E10.MirrorC"),sQuery(id+"F5.wireOp",EDGE,"E11.MirrorC"),sQuery(id+"F5.wireOp",EDGE,"E19.bottom"),sQuery(id+"F5.wireOp",EDGE,"E19.top"),sQuery(id+"F5.wireOp",EDGE,"E19.left"),sQuery(id+"F5.wireOp",EDGE,"E19.right"),sQuery(id+"F5.wireOp",EDGE,"E58")])],"isStart":false}),makeQuery(id+"F9.opExtrude","SWEPT_FACE",FACE,{"disambiguationData":[OSD([sQuery(id+"F5.wireOp",EDGE,"E13")])]})]});
            var Q2;
            Q2=makeQuery(id+"F7.boolean.opBoolean","INTERSECT",EDGE,{"derivedFrom":[makeQuery(id+"F6.opExtrude","CAP_FACE",FACE,{"disambiguationData":[OSD([sQuery(id+"F5.wireOp",EDGE,"E0.bottom"),sQuery(id+"F5.wireOp",EDGE,"E0.top"),sQuery(id+"F5.wireOp",EDGE,"E0.left"),sQuery(id+"F5.wireOp",EDGE,"E0.right"),sQuery(id+"F5.wireOp",EDGE,"E1"),sQuery(id+"F5.wireOp",EDGE,"E2"),sQuery(id+"F5.wireOp",EDGE,"E3"),sQuery(id+"F5.wireOp",EDGE,"E8"),sQuery(id+"F5.wireOp",EDGE,"E9.MirrorC"),sQuery(id+"F5.wireOp",EDGE,"E10.MirrorC"),sQuery(id+"F5.wireOp",EDGE,"E11.MirrorC"),sQuery(id+"F5.wireOp",EDGE,"E19.bottom"),sQuery(id+"F5.wireOp",EDGE,"E19.top"),sQuery(id+"F5.wireOp",EDGE,"E19.left"),sQuery(id+"F5.wireOp",EDGE,"E19.right"),sQuery(id+"F5.wireOp",EDGE,"E58")])],"isStart":false}),makeQuery(id+"F7.opExtrude","SWEPT_FACE",FACE,{"disambiguationData":[OSD([sQuery(id+"F5.wireOp",EDGE,"E12.1")])]})]});
            var Q3;
            Q3=makeQuery(id+"F7.boolean.opBoolean","INTERSECT",EDGE,{"derivedFrom":[makeQuery(id+"F6.opExtrude","CAP_FACE",FACE,{"disambiguationData":[OSD([sQuery(id+"F5.wireOp",EDGE,"E0.bottom"),sQuery(id+"F5.wireOp",EDGE,"E0.top"),sQuery(id+"F5.wireOp",EDGE,"E0.left"),sQuery(id+"F5.wireOp",EDGE,"E0.right"),sQuery(id+"F5.wireOp",EDGE,"E1"),sQuery(id+"F5.wireOp",EDGE,"E2"),sQuery(id+"F5.wireOp",EDGE,"E3"),sQuery(id+"F5.wireOp",EDGE,"E8"),sQuery(id+"F5.wireOp",EDGE,"E9.MirrorC"),sQuery(id+"F5.wireOp",EDGE,"E10.MirrorC"),sQuery(id+"F5.wireOp",EDGE,"E11.MirrorC"),sQuery(id+"F5.wireOp",EDGE,"E19.bottom"),sQuery(id+"F5.wireOp",EDGE,"E19.top"),sQuery(id+"F5.wireOp",EDGE,"E19.left"),sQuery(id+"F5.wireOp",EDGE,"E19.right"),sQuery(id+"F5.wireOp",EDGE,"E58")])],"isStart":false}),makeQuery(id+"F7.opExtrude","SWEPT_FACE",FACE,{"disambiguationData":[OSD([sQuery(id+"F5.wireOp",EDGE,"E12.3")])]})]});
            var Q4;
            Q4=makeQuery(id+"F9.boolean.opBoolean","INTERSECT",EDGE,{"derivedFrom":[makeQuery(id+"F6.opExtrude","CAP_FACE",FACE,{"disambiguationData":[OSD([sQuery(id+"F5.wireOp",EDGE,"E0.bottom"),sQuery(id+"F5.wireOp",EDGE,"E0.top"),sQuery(id+"F5.wireOp",EDGE,"E0.left"),sQuery(id+"F5.wireOp",EDGE,"E0.right"),sQuery(id+"F5.wireOp",EDGE,"E1"),sQuery(id+"F5.wireOp",EDGE,"E2"),sQuery(id+"F5.wireOp",EDGE,"E3"),sQuery(id+"F5.wireOp",EDGE,"E8"),sQuery(id+"F5.wireOp",EDGE,"E9.MirrorC"),sQuery(id+"F5.wireOp",EDGE,"E10.MirrorC"),sQuery(id+"F5.wireOp",EDGE,"E11.MirrorC"),sQuery(id+"F5.wireOp",EDGE,"E19.bottom"),sQuery(id+"F5.wireOp",EDGE,"E19.top"),sQuery(id+"F5.wireOp",EDGE,"E19.left"),sQuery(id+"F5.wireOp",EDGE,"E19.right"),sQuery(id+"F5.wireOp",EDGE,"E58")])],"isStart":false}),makeQuery(id+"F9.opExtrude","SWEPT_FACE",FACE,{"disambiguationData":[OSD([sQuery(id+"F5.wireOp",EDGE,"E15")])]})]});
            var Q5;
            Q5=makeQuery(id+"F9.boolean.opBoolean","INTERSECT",EDGE,{"derivedFrom":[makeQuery(id+"F6.opExtrude","CAP_FACE",FACE,{"disambiguationData":[OSD([sQuery(id+"F5.wireOp",EDGE,"E0.bottom"),sQuery(id+"F5.wireOp",EDGE,"E0.top"),sQuery(id+"F5.wireOp",EDGE,"E0.left"),sQuery(id+"F5.wireOp",EDGE,"E0.right"),sQuery(id+"F5.wireOp",EDGE,"E1"),sQuery(id+"F5.wireOp",EDGE,"E2"),sQuery(id+"F5.wireOp",EDGE,"E3"),sQuery(id+"F5.wireOp",EDGE,"E8"),sQuery(id+"F5.wireOp",EDGE,"E9.MirrorC"),sQuery(id+"F5.wireOp",EDGE,"E10.MirrorC"),sQuery(id+"F5.wireOp",EDGE,"E11.MirrorC"),sQuery(id+"F5.wireOp",EDGE,"E19.bottom"),sQuery(id+"F5.wireOp",EDGE,"E19.top"),sQuery(id+"F5.wireOp",EDGE,"E19.left"),sQuery(id+"F5.wireOp",EDGE,"E19.right"),sQuery(id+"F5.wireOp",EDGE,"E58")])],"isStart":false}),makeQuery(id+"F9.opExtrude","SWEPT_FACE",FACE,{"disambiguationData":[OSD([sQuery(id+"F5.wireOp",EDGE,"E16")])]})]});
            var Q6;
            Q6=makeQuery(id+"F8.boolean.opBoolean","INTERSECT",EDGE,{"derivedFrom":[makeQuery(id+"F6.opExtrude","CAP_FACE",FACE,{"disambiguationData":[OSD([sQuery(id+"F5.wireOp",EDGE,"E0.bottom"),sQuery(id+"F5.wireOp",EDGE,"E0.top"),sQuery(id+"F5.wireOp",EDGE,"E0.left"),sQuery(id+"F5.wireOp",EDGE,"E0.right"),sQuery(id+"F5.wireOp",EDGE,"E1"),sQuery(id+"F5.wireOp",EDGE,"E2"),sQuery(id+"F5.wireOp",EDGE,"E3"),sQuery(id+"F5.wireOp",EDGE,"E8"),sQuery(id+"F5.wireOp",EDGE,"E9.MirrorC"),sQuery(id+"F5.wireOp",EDGE,"E10.MirrorC"),sQuery(id+"F5.wireOp",EDGE,"E11.MirrorC"),sQuery(id+"F5.wireOp",EDGE,"E19.bottom"),sQuery(id+"F5.wireOp",EDGE,"E19.top"),sQuery(id+"F5.wireOp",EDGE,"E19.left"),sQuery(id+"F5.wireOp",EDGE,"E19.right"),sQuery(id+"F5.wireOp",EDGE,"E58")])],"isStart":false}),makeQuery(id+"F8.opExtrude","SWEPT_FACE",FACE,{"disambiguationData":[OSD([sQuery(id+"F5.wireOp",EDGE,"E12.2")])]})]});
            var Q7;
            Q7=makeQuery(id+"F9.boolean.opBoolean","INTERSECT",EDGE,{"derivedFrom":[makeQuery(id+"F6.opExtrude","CAP_FACE",FACE,{"disambiguationData":[OSD([sQuery(id+"F5.wireOp",EDGE,"E0.bottom"),sQuery(id+"F5.wireOp",EDGE,"E0.top"),sQuery(id+"F5.wireOp",EDGE,"E0.left"),sQuery(id+"F5.wireOp",EDGE,"E0.right"),sQuery(id+"F5.wireOp",EDGE,"E1"),sQuery(id+"F5.wireOp",EDGE,"E2"),sQuery(id+"F5.wireOp",EDGE,"E3"),sQuery(id+"F5.wireOp",EDGE,"E8"),sQuery(id+"F5.wireOp",EDGE,"E9.MirrorC"),sQuery(id+"F5.wireOp",EDGE,"E10.MirrorC"),sQuery(id+"F5.wireOp",EDGE,"E11.MirrorC"),sQuery(id+"F5.wireOp",EDGE,"E19.bottom"),sQuery(id+"F5.wireOp",EDGE,"E19.top"),sQuery(id+"F5.wireOp",EDGE,"E19.left"),sQuery(id+"F5.wireOp",EDGE,"E19.right"),sQuery(id+"F5.wireOp",EDGE,"E58")])],"isStart":false}),makeQuery(id+"F9.opExtrude","SWEPT_FACE",FACE,{"disambiguationData":[OSD([sQuery(id+"F5.wireOp",EDGE,"E14")])]})]});
            fillet(context, id + "F44", {"entities" : qUnion([Q0, Q1, Q2, Q3, Q4, Q5, Q6, Q7]), "radius" : 2 * mm, "allowEdgeOverflow" : false});
        }
        {
            var Q0;
            Q0=makeQuery(id+"F19.opExtrude","CAP_EDGE",EDGE,{"disambiguationData":[OSD([sQuery(id+"F5.wireOp",EDGE,"E27")])],"isStart":true});
            var Q1;
            Q1=makeQuery(id+"F19.opExtrude","CAP_EDGE",EDGE,{"disambiguationData":[OSD([sQuery(id+"F5.wireOp",EDGE,"E28.4.0")])],"isStart":true});
            var Q2;
            Q2=makeQuery(id+"F19.opExtrude","CAP_EDGE",EDGE,{"disambiguationData":[OSD([sQuery(id+"F5.wireOp",EDGE,"E28.3.0")])],"isStart":true});
            var Q3;
            Q3=makeQuery(id+"F19.opExtrude","CAP_EDGE",EDGE,{"disambiguationData":[OSD([sQuery(id+"F5.wireOp",EDGE,"E28.2.0")])],"isStart":true});
            var Q4;
            Q4=makeQuery(id+"F19.opExtrude","CAP_EDGE",EDGE,{"disambiguationData":[OSD([sQuery(id+"F5.wireOp",EDGE,"E28.1.0")])],"isStart":true});
            var Q5;
            Q5=makeQuery(id+"F19.opExtrude","CAP_EDGE",EDGE,{"disambiguationData":[OSD([sQuery(id+"F5.wireOp",EDGE,"E22")])],"isStart":true});
            var Q6;
            Q6=makeQuery(id+"F19.opExtrude","CAP_EDGE",EDGE,{"disambiguationData":[OSD([sQuery(id+"F5.wireOp",EDGE,"E59")])],"isStart":true});
            chamfer(context, id + "F45", {"entities" : qUnion([Q0, Q1, Q2, Q3, Q4, Q5, Q6]), "width" : 0.3 * mm, "tangentPropagation" : true});
        }
    });
